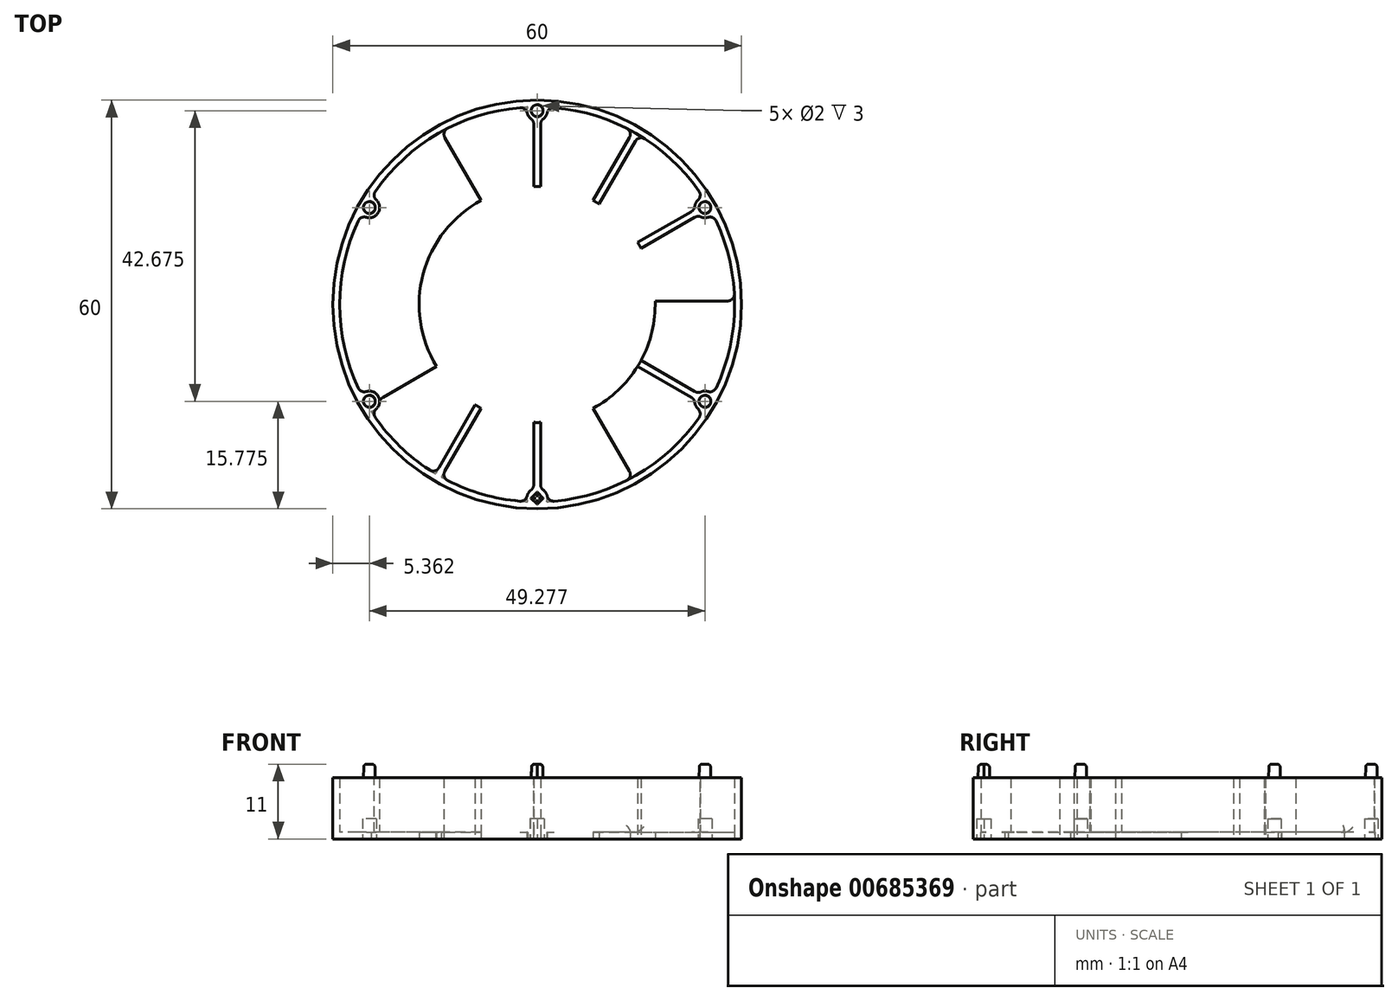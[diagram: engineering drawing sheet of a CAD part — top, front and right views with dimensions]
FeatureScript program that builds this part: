
annotation { "Feature Type Name" : "Feature", "Feature Type Description" : "" }
export const myFeature = defineFeature(function(context is Context, id is Id, definition is map)
    precondition{}
    {
        {
            var Q0;
            Q0=qCreatedBy(makeId("Top.planeOp"),FACE);
            var sketch = newSketch(context, id + "F0", { "sketchPlane" : qUnion([Q0])});
            skCircle(sketch, "E0", {"center": v(0, 0) * mm, "radius": 30 * mm});
            skCircle(sketch, "E1.0", {"center": v(0, 0) * mm, "radius": 29 * mm});
            skLineSegment(sketch, "E2.bottom", {"start": v(14.56, 26.23) * mm, "end": v(15.43, 25.73) * mm});
            skLineSegment(sketch, "E2.top", {"start": v(-15.43, -25.73) * mm, "end": v(-14.56, -26.23) * mm});
            skLineSegment(sketch, "E2.left", {"start": v(14.56, 26.23) * mm, "end": v(-15.43, -25.73) * mm});
            skLineSegment(sketch, "E2.right", {"start": v(15.43, 25.73) * mm, "end": v(-14.56, -26.23) * mm});
            skLineSegment(sketch, "E3.bottom", {"start": v(25.73, 15.43) * mm, "end": v(26.23, 14.56) * mm});
            skLineSegment(sketch, "E3.top", {"start": v(-26.23, -14.56) * mm, "end": v(-25.73, -15.43) * mm});
            skLineSegment(sketch, "E3.left", {"start": v(25.73, 15.43) * mm, "end": v(-26.23, -14.56) * mm});
            skLineSegment(sketch, "E3.right", {"start": v(26.23, 14.56) * mm, "end": v(-25.73, -15.43) * mm});
            skLineSegment(sketch, "E4", {"start": v(-38.35, 0) * mm, "end": v(39.17, 0) * mm, "construction": true});
            skLineSegment(sketch, "E5", {"start": v(0, 42.5) * mm, "end": v(0, -42.47) * mm, "construction": true});
            skLineSegment(sketch, "E6.bottom", {"start": v(-30, 0.5) * mm, "end": v(30, 0.5) * mm});
            skLineSegment(sketch, "E6.top", {"start": v(-30, -0.5) * mm, "end": v(30, -0.5) * mm});
            skLineSegment(sketch, "E6.left", {"start": v(-30, 0.5) * mm, "end": v(-30, -0.5) * mm});
            skLineSegment(sketch, "E6.right", {"start": v(30, 0.5) * mm, "end": v(30, -0.5) * mm});
            skLineSegment(sketch, "E7.bottom", {"start": v(-25.73, 15.43) * mm, "end": v(26.23, -14.56) * mm});
            skLineSegment(sketch, "E7.top", {"start": v(-26.23, 14.56) * mm, "end": v(25.73, -15.43) * mm});
            skLineSegment(sketch, "E7.left", {"start": v(-25.73, 15.43) * mm, "end": v(-26.23, 14.56) * mm});
            skLineSegment(sketch, "E7.right", {"start": v(26.23, -14.56) * mm, "end": v(25.73, -15.43) * mm});
            skLineSegment(sketch, "E8.bottom", {"start": v(-0.5, 30) * mm, "end": v(0.5, 30) * mm});
            skLineSegment(sketch, "E8.top", {"start": v(-0.5, -30) * mm, "end": v(0.5, -30) * mm});
            skLineSegment(sketch, "E8.left", {"start": v(-0.5, 30) * mm, "end": v(-0.5, -30) * mm});
            skLineSegment(sketch, "E8.right", {"start": v(0.5, 30) * mm, "end": v(0.5, -30) * mm});
            skLineSegment(sketch, "E9.bottom", {"start": v(-15.43, 25.73) * mm, "end": v(-14.56, 26.23) * mm});
            skLineSegment(sketch, "E9.top", {"start": v(14.56, -26.23) * mm, "end": v(15.43, -25.73) * mm});
            skLineSegment(sketch, "E9.left", {"start": v(-15.43, 25.73) * mm, "end": v(14.56, -26.23) * mm});
            skLineSegment(sketch, "E9.right", {"start": v(-14.56, 26.23) * mm, "end": v(15.43, -25.73) * mm});
            skCircle(sketch, "E10", {"center": v(0, 0) * mm, "radius": 17.33 * mm});
            skSolve(sketch);
        }
        {
            var Q0;
            Q0=qCreatedBy(makeId("Top.planeOp"),FACE);
            var sketch = newSketch(context, id + "F1", { "sketchPlane" : qUnion([Q0])});
            skCircle(sketch, "E11", {"center": v(0, 0) * mm, "radius": 30 * mm});
            skCircle(sketch, "E12", {"center": v(0, 0) * mm, "radius": 29 * mm});
            skSolve(sketch);
        }
        {
            var Q0;
            Q0=makeQuery(id+"F1.imprint","IMPRINT",FACE,{"disambiguationData":[TD([[makeQuery(id+"F1.imprint","IMPRINT",EDGE,{"derivedFrom":sQuery(id+"F1.wireOp",EDGE,"E11")}),1.0]])]});
            extrude(context, id + "F2", {"entities" : qUnion([Q0]), "depth" : 9 * mm, "offsetDistance" : 25 * mm});
        }
        {
            var Q0;
            {var subQ0=sQuery(id+"F0.wireOp",EDGE,"E8.left");var subQ1=sQuery(id+"F0.wireOp",EDGE,"E1.0");var subQ2=makeQuery(id+"F0.imprint","INTERSECT",VERTEX,{"disambiguationData":[OD(1.0)],"derivedFrom":[subQ1,subQ0]});Q0=makeQuery(id+"F0.imprint","IMPRINT",FACE,{"disambiguationData":[TD([[makeQuery(id+"F0.imprint","IMPRINT",EDGE,{"disambiguationData":[TD([[subQ2,-1.0]])],"derivedFrom":subQ1}),1.0]])]});}
            var Q1;
            {var subQ0=sQuery(id+"F0.wireOp",EDGE,"E8.right");var subQ1=sQuery(id+"F0.wireOp",EDGE,"E1.0");var subQ2=makeQuery(id+"F0.imprint","INTERSECT",VERTEX,{"disambiguationData":[OD(0.0)],"derivedFrom":[subQ1,subQ0]});Q1=makeQuery(id+"F0.imprint","IMPRINT",FACE,{"disambiguationData":[TD([[makeQuery(id+"F0.imprint","IMPRINT",EDGE,{"disambiguationData":[TD([[subQ2,-1.0]])],"derivedFrom":subQ1}),1.0]])]});}
            var Q2;
            {var subQ0=sQuery(id+"F0.wireOp",EDGE,"E3.right");var subQ1=sQuery(id+"F0.wireOp",EDGE,"E1.0");var subQ2=makeQuery(id+"F0.imprint","INTERSECT",VERTEX,{"disambiguationData":[OD(0.0)],"derivedFrom":[subQ1,subQ0]});Q2=makeQuery(id+"F0.imprint","IMPRINT",FACE,{"disambiguationData":[TD([[makeQuery(id+"F0.imprint","IMPRINT",EDGE,{"disambiguationData":[TD([[subQ2,-1.0]])],"derivedFrom":subQ1}),1.0]])]});}
            var Q3;
            {var subQ0=sQuery(id+"F0.wireOp",EDGE,"E7.top");var subQ1=sQuery(id+"F0.wireOp",EDGE,"E1.0");var subQ2=makeQuery(id+"F0.imprint","INTERSECT",VERTEX,{"disambiguationData":[OD(1.0)],"derivedFrom":[subQ1,subQ0]});Q3=makeQuery(id+"F0.imprint","IMPRINT",FACE,{"disambiguationData":[TD([[makeQuery(id+"F0.imprint","IMPRINT",EDGE,{"disambiguationData":[TD([[subQ2,-1.0]])],"derivedFrom":subQ1}),1.0]])]});}
            var Q4;
            {var subQ0=sQuery(id+"F0.wireOp",EDGE,"E2.left");var subQ1=sQuery(id+"F0.wireOp",EDGE,"E1.0");var subQ2=makeQuery(id+"F0.imprint","INTERSECT",VERTEX,{"disambiguationData":[OD(1.0)],"derivedFrom":[subQ1,subQ0]});Q4=makeQuery(id+"F0.imprint","IMPRINT",FACE,{"disambiguationData":[TD([[makeQuery(id+"F0.imprint","IMPRINT",EDGE,{"disambiguationData":[TD([[subQ2,-1.0]])],"derivedFrom":subQ1}),1.0]])]});}
            extrude(context, id + "F3", {"entities" : qUnion([Q0, Q1, Q2, Q3, Q4]), "operationType" : NewBodyOperationType.ADD, "depth" : 9 * mm, "offsetDistance" : 25 * mm});
        }
        {
            var Q0;
            Q0=makeQuery(id+"F1.imprint","IMPRINT",FACE,{"disambiguationData":[TD([[makeQuery(id+"F1.imprint","IMPRINT",EDGE,{"derivedFrom":sQuery(id+"F1.wireOp",EDGE,"E11")}),1.0]])]});
            var Q1;
            Q1=makeQuery(id+"F1.imprint","IMPRINT",FACE,{"disambiguationData":[TD([[makeQuery(id+"F1.imprint","IMPRINT",EDGE,{"derivedFrom":sQuery(id+"F1.wireOp",EDGE,"E12")}),1.0]])]});
            extrude(context, id + "F4", {"entities" : qUnion([Q0, Q1]), "operationType" : NewBodyOperationType.ADD, "depth" : 1 * mm, "offsetDistance" : 25 * mm});
        }
        {
            var Q0;
            {var subQ0=sQuery(id+"F0.wireOp",EDGE,"E8.right");var subQ1=sQuery(id+"F0.wireOp",EDGE,"E1.0");var subQ2=makeQuery(id+"F0.imprint","INTERSECT",VERTEX,{"disambiguationData":[OD(1.0)],"derivedFrom":[subQ1,subQ0]});Q0=makeQuery(id+"F0.imprint","IMPRINT",FACE,{"disambiguationData":[TD([[makeQuery(id+"F0.imprint","IMPRINT",EDGE,{"disambiguationData":[TD([[subQ2,-1.0]])],"derivedFrom":subQ1}),1.0]])]});}
            var Q1;
            {var subQ0=sQuery(id+"F0.wireOp",EDGE,"E3.right");var subQ1=sQuery(id+"F0.wireOp",EDGE,"E1.0");var subQ2=makeQuery(id+"F0.imprint","INTERSECT",VERTEX,{"disambiguationData":[OD(0.0)],"derivedFrom":[subQ1,subQ0]});Q1=makeQuery(id+"F0.imprint","IMPRINT",FACE,{"disambiguationData":[TD([[makeQuery(id+"F0.imprint","IMPRINT",EDGE,{"disambiguationData":[TD([[subQ2,1.0]])],"derivedFrom":subQ1}),1.0]])]});}
            var Q2;
            {var subQ0=sQuery(id+"F0.wireOp",EDGE,"E3.left");var subQ1=sQuery(id+"F0.wireOp",EDGE,"E1.0");var subQ2=makeQuery(id+"F0.imprint","INTERSECT",VERTEX,{"disambiguationData":[OD(0.0)],"derivedFrom":[subQ1,subQ0]});Q2=makeQuery(id+"F0.imprint","IMPRINT",FACE,{"disambiguationData":[TD([[makeQuery(id+"F0.imprint","IMPRINT",EDGE,{"disambiguationData":[TD([[subQ2,-1.0]])],"derivedFrom":subQ1}),1.0]])]});}
            var Q3;
            {var subQ0=sQuery(id+"F0.wireOp",EDGE,"E2.left");var subQ1=sQuery(id+"F0.wireOp",EDGE,"E1.0");var subQ2=makeQuery(id+"F0.imprint","INTERSECT",VERTEX,{"disambiguationData":[OD(0.0)],"derivedFrom":[subQ1,subQ0]});Q3=makeQuery(id+"F0.imprint","IMPRINT",FACE,{"disambiguationData":[TD([[makeQuery(id+"F0.imprint","IMPRINT",EDGE,{"disambiguationData":[TD([[subQ2,-1.0]])],"derivedFrom":subQ1}),1.0]])]});}
            var Q4;
            {var subQ0=sQuery(id+"F0.wireOp",EDGE,"E8.left");var subQ1=sQuery(id+"F0.wireOp",EDGE,"E1.0");var subQ2=makeQuery(id+"F0.imprint","INTERSECT",VERTEX,{"disambiguationData":[OD(0.0)],"derivedFrom":[subQ1,subQ0]});Q4=makeQuery(id+"F0.imprint","IMPRINT",FACE,{"disambiguationData":[TD([[makeQuery(id+"F0.imprint","IMPRINT",EDGE,{"disambiguationData":[TD([[subQ2,-1.0]])],"derivedFrom":subQ1}),1.0]])]});}
            var Q5;
            {var subQ0=sQuery(id+"F0.wireOp",EDGE,"E3.right");var subQ1=sQuery(id+"F0.wireOp",EDGE,"E1.0");var subQ2=makeQuery(id+"F0.imprint","INTERSECT",VERTEX,{"disambiguationData":[OD(1.0)],"derivedFrom":[subQ1,subQ0]});Q5=makeQuery(id+"F0.imprint","IMPRINT",FACE,{"disambiguationData":[TD([[makeQuery(id+"F0.imprint","IMPRINT",EDGE,{"disambiguationData":[TD([[subQ2,-1.0]])],"derivedFrom":subQ1}),1.0]])]});}
            var Q6;
            {var subQ0=sQuery(id+"F0.wireOp",EDGE,"E2.right");var subQ1=sQuery(id+"F0.wireOp",EDGE,"E1.0");var subQ2=makeQuery(id+"F0.imprint","INTERSECT",VERTEX,{"disambiguationData":[OD(1.0)],"derivedFrom":[subQ1,subQ0]});Q6=makeQuery(id+"F0.imprint","IMPRINT",FACE,{"disambiguationData":[TD([[makeQuery(id+"F0.imprint","IMPRINT",EDGE,{"disambiguationData":[TD([[subQ2,-1.0]])],"derivedFrom":subQ1}),1.0]])]});}
            extrude(context, id + "F5", {"entities" : qUnion([Q0, Q1, Q2, Q3, Q4, Q5, Q6]), "operationType" : NewBodyOperationType.REMOVE, "depth" : 1 * mm, "offsetDistance" : 25 * mm});
        }
        {
            var Q0;
            Q0=qCreatedBy(makeId("Top.planeOp"),FACE);
            var sketch = newSketch(context, id + "F6", { "sketchPlane" : qUnion([Q0])});
            skCircle(sketch, "E13", {"center": v(0, 0) * mm, "radius": 28.45 * mm});
            skLineSegment(sketch, "E14", {"start": v(0, 28.45) * mm, "end": v(0, -28.45) * mm, "construction": true});
            skLineSegment(sketch, "E15", {"start": v(24.64, 14.22) * mm, "end": v(0, 0) * mm, "construction": true});
            skLineSegment(sketch, "E16", {"start": v(14.23, 24.64) * mm, "end": v(0, 0) * mm, "construction": true});
            skLineSegment(sketch, "E17", {"start": v(0, 0) * mm, "end": v(28.45, 0) * mm, "construction": true});
            skLineSegment(sketch, "E18", {"start": v(0, 0) * mm, "end": v(24.64, -14.22) * mm, "construction": true});
            skLineSegment(sketch, "E19", {"start": v(0, 0) * mm, "end": v(14.23, -24.64) * mm, "construction": true});
            skLineSegment(sketch, "E20", {"start": v(0, 0) * mm, "end": v(-14.23, 24.64) * mm, "construction": true});
            skLineSegment(sketch, "E21", {"start": v(0, 0) * mm, "end": v(-24.64, 14.22) * mm, "construction": true});
            skLineSegment(sketch, "E22", {"start": v(0, 0) * mm, "end": v(-28.45, 0) * mm, "construction": true});
            skLineSegment(sketch, "E23", {"start": v(0, 0) * mm, "end": v(-24.64, -14.23) * mm, "construction": true});
            skLineSegment(sketch, "E24", {"start": v(0, 0) * mm, "end": v(-14.22, -24.64) * mm, "construction": true});
            skCircle(sketch, "E25", {"center": v(0, 28.45) * mm, "radius": 1.5 * mm});
            skCircle(sketch, "E26", {"center": v(24.64, 14.22) * mm, "radius": 1.5 * mm});
            skCircle(sketch, "E27", {"center": v(24.64, -14.22) * mm, "radius": 1.5 * mm});
            skCircle(sketch, "E28", {"center": v(0, -28.45) * mm, "radius": 1.5 * mm});
            skCircle(sketch, "E29", {"center": v(-24.64, -14.23) * mm, "radius": 1.5 * mm});
            skCircle(sketch, "E30", {"center": v(-24.64, 14.22) * mm, "radius": 1.5 * mm});
            skCircle(sketch, "E31", {"center": v(-24.64, 14.22) * mm, "radius": 1 * mm});
            skCircle(sketch, "E32", {"center": v(0, 28.45) * mm, "radius": 1 * mm});
            skCircle(sketch, "E33", {"center": v(24.64, 14.22) * mm, "radius": 1 * mm});
            skCircle(sketch, "E34", {"center": v(24.64, -14.22) * mm, "radius": 1 * mm});
            skCircle(sketch, "E35", {"center": v(-24.64, -14.23) * mm, "radius": 1 * mm});
            skLineSegment(sketch, "E36.bottom", {"start": v(1.06, -28.45) * mm, "end": v(0, -29.51) * mm});
            skLineSegment(sketch, "E36.top", {"start": v(0, -27.39) * mm, "end": v(-1.06, -28.45) * mm});
            skLineSegment(sketch, "E36.left", {"start": v(1.06, -28.45) * mm, "end": v(0, -27.39) * mm});
            skLineSegment(sketch, "E36.right", {"start": v(0, -29.51) * mm, "end": v(-1.06, -28.45) * mm});
            skSolve(sketch);
        }
        {
            var Q0;
            {var subQ0=sQuery(id+"F6.wireOp",EDGE,"E30");var subQ1=sQuery(id+"F6.wireOp",EDGE,"E13");var subQ2=makeQuery(id+"F6.imprint","INTERSECT",VERTEX,{"disambiguationData":[OD(0.0)],"derivedFrom":[subQ1,subQ0]});Q0=makeQuery(id+"F6.imprint","IMPRINT",FACE,{"disambiguationData":[TD([[makeQuery(id+"F6.imprint","IMPRINT",EDGE,{"disambiguationData":[TD([[subQ2,-1.0]])],"derivedFrom":subQ1}),1.0]])]});}
            var Q1;
            {var subQ0=sQuery(id+"F6.wireOp",EDGE,"E30");var subQ1=sQuery(id+"F6.wireOp",EDGE,"E13");var subQ2=makeQuery(id+"F6.imprint","INTERSECT",VERTEX,{"disambiguationData":[OD(0.0)],"derivedFrom":[subQ1,subQ0]});Q1=makeQuery(id+"F6.imprint","IMPRINT",FACE,{"disambiguationData":[TD([[makeQuery(id+"F6.imprint","IMPRINT",EDGE,{"disambiguationData":[TD([[subQ2,-1.0]])],"derivedFrom":subQ1}),-1.0]])]});}
            var Q2;
            {var subQ0=sQuery(id+"F6.wireOp",EDGE,"E25");var subQ1=sQuery(id+"F6.wireOp",EDGE,"E13");var subQ2=makeQuery(id+"F6.imprint","INTERSECT",VERTEX,{"disambiguationData":[OD(0.0)],"derivedFrom":[subQ1,subQ0]});Q2=makeQuery(id+"F6.imprint","IMPRINT",FACE,{"disambiguationData":[TD([[makeQuery(id+"F6.imprint","IMPRINT",EDGE,{"disambiguationData":[TD([[subQ2,-1.0]])],"derivedFrom":subQ1}),1.0]])]});}
            var Q3;
            {var subQ0=sQuery(id+"F6.wireOp",EDGE,"E25");var subQ1=sQuery(id+"F6.wireOp",EDGE,"E13");var subQ2=makeQuery(id+"F6.imprint","INTERSECT",VERTEX,{"disambiguationData":[OD(0.0)],"derivedFrom":[subQ1,subQ0]});Q3=makeQuery(id+"F6.imprint","IMPRINT",FACE,{"disambiguationData":[TD([[makeQuery(id+"F6.imprint","IMPRINT",EDGE,{"disambiguationData":[TD([[subQ2,-1.0]])],"derivedFrom":subQ1}),-1.0]])]});}
            var Q4;
            {var subQ0=sQuery(id+"F6.wireOp",EDGE,"E26");var subQ1=sQuery(id+"F6.wireOp",EDGE,"E13");var subQ2=makeQuery(id+"F6.imprint","INTERSECT",VERTEX,{"disambiguationData":[OD(0.0)],"derivedFrom":[subQ1,subQ0]});Q4=makeQuery(id+"F6.imprint","IMPRINT",FACE,{"disambiguationData":[TD([[makeQuery(id+"F6.imprint","IMPRINT",EDGE,{"disambiguationData":[TD([[subQ2,-1.0]])],"derivedFrom":subQ1}),-1.0]])]});}
            var Q5;
            {var subQ0=sQuery(id+"F6.wireOp",EDGE,"E26");var subQ1=sQuery(id+"F6.wireOp",EDGE,"E13");var subQ2=makeQuery(id+"F6.imprint","INTERSECT",VERTEX,{"disambiguationData":[OD(0.0)],"derivedFrom":[subQ1,subQ0]});Q5=makeQuery(id+"F6.imprint","IMPRINT",FACE,{"disambiguationData":[TD([[makeQuery(id+"F6.imprint","IMPRINT",EDGE,{"disambiguationData":[TD([[subQ2,-1.0]])],"derivedFrom":subQ1}),1.0]])]});}
            var Q6;
            {var subQ0=sQuery(id+"F6.wireOp",EDGE,"E29");var subQ1=sQuery(id+"F6.wireOp",EDGE,"E13");var subQ2=makeQuery(id+"F6.imprint","INTERSECT",VERTEX,{"disambiguationData":[OD(0.0)],"derivedFrom":[subQ1,subQ0]});Q6=makeQuery(id+"F6.imprint","IMPRINT",FACE,{"disambiguationData":[TD([[makeQuery(id+"F6.imprint","IMPRINT",EDGE,{"disambiguationData":[TD([[subQ2,-1.0]])],"derivedFrom":subQ1}),1.0]])]});}
            var Q7;
            {var subQ0=sQuery(id+"F6.wireOp",EDGE,"E29");var subQ1=sQuery(id+"F6.wireOp",EDGE,"E13");var subQ2=makeQuery(id+"F6.imprint","INTERSECT",VERTEX,{"disambiguationData":[OD(0.0)],"derivedFrom":[subQ1,subQ0]});Q7=makeQuery(id+"F6.imprint","IMPRINT",FACE,{"disambiguationData":[TD([[makeQuery(id+"F6.imprint","IMPRINT",EDGE,{"disambiguationData":[TD([[subQ2,-1.0]])],"derivedFrom":subQ1}),-1.0]])]});}
            var Q8;
            {var subQ3=sQuery(id+"F6.wireOp",EDGE,"E13");var subQ5=sQuery(id+"F6.wireOp",EDGE,"E28");var subQ6=makeQuery(id+"F6.imprint","INTERSECT",VERTEX,{"disambiguationData":[OD(0.0)],"derivedFrom":[subQ3,subQ5]});Q8=makeQuery(id+"F6.imprint","IMPRINT",FACE,{"disambiguationData":[TD([[makeQuery(id+"F6.imprint","IMPRINT",EDGE,{"disambiguationData":[TD([[subQ6,-1.0]])],"derivedFrom":subQ3}),1.0]])]});}
            var Q9;
            {var subQ6=sQuery(id+"F6.wireOp",EDGE,"E36.bottom");Q9=makeQuery(id+"F6.imprint","IMPRINT",FACE,{"disambiguationData":[TD([[makeQuery(id+"F6.imprint","IMPRINT",EDGE,{"derivedFrom":subQ6}),1.0]])]});}
            var Q10;
            {var subQ0=sQuery(id+"F6.wireOp",EDGE,"E27");var subQ1=sQuery(id+"F6.wireOp",EDGE,"E13");var subQ2=makeQuery(id+"F6.imprint","INTERSECT",VERTEX,{"disambiguationData":[OD(0.0)],"derivedFrom":[subQ1,subQ0]});Q10=makeQuery(id+"F6.imprint","IMPRINT",FACE,{"disambiguationData":[TD([[makeQuery(id+"F6.imprint","IMPRINT",EDGE,{"disambiguationData":[TD([[subQ2,-1.0]])],"derivedFrom":subQ1}),-1.0]])]});}
            var Q11;
            {var subQ0=sQuery(id+"F6.wireOp",EDGE,"E27");var subQ1=sQuery(id+"F6.wireOp",EDGE,"E13");var subQ2=makeQuery(id+"F6.imprint","INTERSECT",VERTEX,{"disambiguationData":[OD(0.0)],"derivedFrom":[subQ1,subQ0]});Q11=makeQuery(id+"F6.imprint","IMPRINT",FACE,{"disambiguationData":[TD([[makeQuery(id+"F6.imprint","IMPRINT",EDGE,{"disambiguationData":[TD([[subQ2,-1.0]])],"derivedFrom":subQ1}),1.0]])]});}
            var Q12;
            {var subQ0=sQuery(id+"F6.wireOp",EDGE,"E31");var subQ1=sQuery(id+"F6.wireOp",EDGE,"E13");var subQ2=makeQuery(id+"F6.imprint","INTERSECT",VERTEX,{"disambiguationData":[OD(0.0)],"derivedFrom":[subQ1,subQ0]});Q12=makeQuery(id+"F6.imprint","IMPRINT",FACE,{"disambiguationData":[TD([[makeQuery(id+"F6.imprint","IMPRINT",EDGE,{"disambiguationData":[TD([[subQ2,-1.0]])],"derivedFrom":subQ1}),1.0]])]});}
            var Q13;
            {var subQ0=sQuery(id+"F6.wireOp",EDGE,"E31");var subQ1=sQuery(id+"F6.wireOp",EDGE,"E13");var subQ2=makeQuery(id+"F6.imprint","INTERSECT",VERTEX,{"disambiguationData":[OD(0.0)],"derivedFrom":[subQ1,subQ0]});Q13=makeQuery(id+"F6.imprint","IMPRINT",FACE,{"disambiguationData":[TD([[makeQuery(id+"F6.imprint","IMPRINT",EDGE,{"disambiguationData":[TD([[subQ2,-1.0]])],"derivedFrom":subQ1}),-1.0]])]});}
            var Q14;
            {var subQ0=sQuery(id+"F6.wireOp",EDGE,"E32");var subQ1=sQuery(id+"F6.wireOp",EDGE,"E13");var subQ2=makeQuery(id+"F6.imprint","INTERSECT",VERTEX,{"disambiguationData":[OD(0.0)],"derivedFrom":[subQ1,subQ0]});Q14=makeQuery(id+"F6.imprint","IMPRINT",FACE,{"disambiguationData":[TD([[makeQuery(id+"F6.imprint","IMPRINT",EDGE,{"disambiguationData":[TD([[subQ2,-1.0]])],"derivedFrom":subQ1}),-1.0]])]});}
            var Q15;
            {var subQ0=sQuery(id+"F6.wireOp",EDGE,"E32");var subQ1=sQuery(id+"F6.wireOp",EDGE,"E13");var subQ2=makeQuery(id+"F6.imprint","INTERSECT",VERTEX,{"disambiguationData":[OD(0.0)],"derivedFrom":[subQ1,subQ0]});Q15=makeQuery(id+"F6.imprint","IMPRINT",FACE,{"disambiguationData":[TD([[makeQuery(id+"F6.imprint","IMPRINT",EDGE,{"disambiguationData":[TD([[subQ2,-1.0]])],"derivedFrom":subQ1}),1.0]])]});}
            var Q16;
            {var subQ0=sQuery(id+"F6.wireOp",EDGE,"E33");var subQ1=sQuery(id+"F6.wireOp",EDGE,"E13");var subQ2=makeQuery(id+"F6.imprint","INTERSECT",VERTEX,{"disambiguationData":[OD(0.0)],"derivedFrom":[subQ1,subQ0]});Q16=makeQuery(id+"F6.imprint","IMPRINT",FACE,{"disambiguationData":[TD([[makeQuery(id+"F6.imprint","IMPRINT",EDGE,{"disambiguationData":[TD([[subQ2,-1.0]])],"derivedFrom":subQ1}),-1.0]])]});}
            var Q17;
            {var subQ0=sQuery(id+"F6.wireOp",EDGE,"E33");var subQ1=sQuery(id+"F6.wireOp",EDGE,"E13");var subQ2=makeQuery(id+"F6.imprint","INTERSECT",VERTEX,{"disambiguationData":[OD(0.0)],"derivedFrom":[subQ1,subQ0]});Q17=makeQuery(id+"F6.imprint","IMPRINT",FACE,{"disambiguationData":[TD([[makeQuery(id+"F6.imprint","IMPRINT",EDGE,{"disambiguationData":[TD([[subQ2,-1.0]])],"derivedFrom":subQ1}),1.0]])]});}
            var Q18;
            {var subQ0=sQuery(id+"F6.wireOp",EDGE,"E34");var subQ1=sQuery(id+"F6.wireOp",EDGE,"E13");var subQ2=makeQuery(id+"F6.imprint","INTERSECT",VERTEX,{"disambiguationData":[OD(0.0)],"derivedFrom":[subQ1,subQ0]});Q18=makeQuery(id+"F6.imprint","IMPRINT",FACE,{"disambiguationData":[TD([[makeQuery(id+"F6.imprint","IMPRINT",EDGE,{"disambiguationData":[TD([[subQ2,-1.0]])],"derivedFrom":subQ1}),-1.0]])]});}
            var Q19;
            {var subQ0=sQuery(id+"F6.wireOp",EDGE,"E34");var subQ1=sQuery(id+"F6.wireOp",EDGE,"E13");var subQ2=makeQuery(id+"F6.imprint","INTERSECT",VERTEX,{"disambiguationData":[OD(0.0)],"derivedFrom":[subQ1,subQ0]});Q19=makeQuery(id+"F6.imprint","IMPRINT",FACE,{"disambiguationData":[TD([[makeQuery(id+"F6.imprint","IMPRINT",EDGE,{"disambiguationData":[TD([[subQ2,-1.0]])],"derivedFrom":subQ1}),1.0]])]});}
            var Q20;
            {var subQ1=sQuery(id+"F6.wireOp",EDGE,"E36.bottom");Q20=makeQuery(id+"F6.imprint","IMPRINT",FACE,{"disambiguationData":[TD([[makeQuery(id+"F6.imprint","IMPRINT",EDGE,{"derivedFrom":subQ1}),-1.0]])]});}
            var Q21;
            {var subQ0=sQuery(id+"F6.wireOp",EDGE,"E35");var subQ1=sQuery(id+"F6.wireOp",EDGE,"E13");var subQ2=makeQuery(id+"F6.imprint","INTERSECT",VERTEX,{"disambiguationData":[OD(0.0)],"derivedFrom":[subQ1,subQ0]});Q21=makeQuery(id+"F6.imprint","IMPRINT",FACE,{"disambiguationData":[TD([[makeQuery(id+"F6.imprint","IMPRINT",EDGE,{"disambiguationData":[TD([[subQ2,-1.0]])],"derivedFrom":subQ1}),-1.0]])]});}
            var Q22;
            {var subQ0=sQuery(id+"F6.wireOp",EDGE,"E35");var subQ1=sQuery(id+"F6.wireOp",EDGE,"E13");var subQ2=makeQuery(id+"F6.imprint","INTERSECT",VERTEX,{"disambiguationData":[OD(0.0)],"derivedFrom":[subQ1,subQ0]});Q22=makeQuery(id+"F6.imprint","IMPRINT",FACE,{"disambiguationData":[TD([[makeQuery(id+"F6.imprint","IMPRINT",EDGE,{"disambiguationData":[TD([[subQ2,-1.0]])],"derivedFrom":subQ1}),1.0]])]});}
            var Q23;
            {var subQ0=sQuery(id+"F6.wireOp",EDGE,"E36.top");var subQ1=sQuery(id+"F6.wireOp",EDGE,"E13");var subQ2=makeQuery(id+"F6.imprint","INTERSECT",VERTEX,{"derivedFrom":[subQ1,subQ0]});Q23=makeQuery(id+"F6.imprint","IMPRINT",FACE,{"disambiguationData":[TD([[makeQuery(id+"F6.imprint","IMPRINT",EDGE,{"disambiguationData":[TD([[subQ2,-1.0]])],"derivedFrom":subQ1}),1.0]])]});}
            extrude(context, id + "F7", {"entities" : qUnion([Q0, Q1, Q2, Q3, Q4, Q5, Q6, Q7, Q8, Q9, Q10, Q11, Q12, Q13, Q14, Q15, Q16, Q17, Q18, Q19, Q20, Q21, Q22, Q23]), "operationType" : NewBodyOperationType.ADD, "depth" : 9 * mm, "offsetDistance" : 25 * mm});
        }
        {
            var Q0;
            {var subQ0=sQuery(id+"F0.wireOp",EDGE,"E8.right");var subQ1=sQuery(id+"F0.wireOp",EDGE,"E1.0");Q0=makeQuery(id+"F3.opExtrude","SWEPT_EDGE",EDGE,{"disambiguationData":[OSD([subQ1,subQ0]),TDD([makeQuery(id+"F0.imprint","INTERSECT",VERTEX,{"disambiguationData":[OD(1.0)],"derivedFrom":[subQ1,subQ0]})])]});}
            var Q1;
            {var subQ0=sQuery(id+"F0.wireOp",EDGE,"E2.left");var subQ1=sQuery(id+"F0.wireOp",EDGE,"E1.0");Q1=makeQuery(id+"F3.opExtrude","SWEPT_EDGE",EDGE,{"disambiguationData":[OSD([subQ1,subQ0]),TDD([makeQuery(id+"F0.imprint","INTERSECT",VERTEX,{"disambiguationData":[OD(1.0)],"derivedFrom":[subQ1,subQ0]})])]});}
            var Q2;
            {var subQ0=sQuery(id+"F0.wireOp",EDGE,"E3.left");var subQ1=sQuery(id+"F0.wireOp",EDGE,"E1.0");Q2=makeQuery(id+"F3.opExtrude","SWEPT_EDGE",EDGE,{"disambiguationData":[OSD([subQ1,subQ0]),TDD([makeQuery(id+"F0.imprint","INTERSECT",VERTEX,{"disambiguationData":[OD(1.0)],"derivedFrom":[subQ1,subQ0]})])]});}
            var Q3;
            {var subQ0=sQuery(id+"F0.wireOp",EDGE,"E6.bottom");var subQ1=sQuery(id+"F0.wireOp",EDGE,"E1.0");Q3=makeQuery(id+"F3.opExtrude","SWEPT_EDGE",EDGE,{"disambiguationData":[OSD([subQ1,subQ0]),TDD([makeQuery(id+"F0.imprint","INTERSECT",VERTEX,{"disambiguationData":[OD(1.0)],"derivedFrom":[subQ1,subQ0]})])]});}
            var Q4;
            {var subQ0=sQuery(id+"F0.wireOp",EDGE,"E9.right");var subQ1=sQuery(id+"F0.wireOp",EDGE,"E1.0");Q4=makeQuery(id+"F3.opExtrude","SWEPT_EDGE",EDGE,{"disambiguationData":[OSD([subQ1,subQ0]),TDD([makeQuery(id+"F0.imprint","INTERSECT",VERTEX,{"disambiguationData":[OD(1.0)],"derivedFrom":[subQ1,subQ0]})])]});}
            var Q5;
            {var subQ0=sQuery(id+"F0.wireOp",EDGE,"E7.bottom");var subQ1=sQuery(id+"F0.wireOp",EDGE,"E1.0");Q5=makeQuery(id+"F3.opExtrude","SWEPT_EDGE",EDGE,{"disambiguationData":[OSD([subQ1,subQ0]),TDD([makeQuery(id+"F0.imprint","INTERSECT",VERTEX,{"disambiguationData":[OD(1.0)],"derivedFrom":[subQ1,subQ0]})])]});}
            var Q6;
            {var subQ0=sQuery(id+"F0.wireOp",EDGE,"E8.left");var subQ1=sQuery(id+"F0.wireOp",EDGE,"E1.0");Q6=makeQuery(id+"F3.opExtrude","SWEPT_EDGE",EDGE,{"disambiguationData":[OSD([subQ1,subQ0]),TDD([makeQuery(id+"F0.imprint","INTERSECT",VERTEX,{"disambiguationData":[OD(0.0)],"derivedFrom":[subQ1,subQ0]})])]});}
            var Q7;
            {var subQ0=sQuery(id+"F0.wireOp",EDGE,"E2.left");var subQ1=sQuery(id+"F0.wireOp",EDGE,"E1.0");Q7=makeQuery(id+"F3.opExtrude","SWEPT_EDGE",EDGE,{"disambiguationData":[OSD([subQ1,subQ0]),TDD([makeQuery(id+"F0.imprint","INTERSECT",VERTEX,{"disambiguationData":[OD(0.0)],"derivedFrom":[subQ1,subQ0]})])]});}
            var Q8;
            {var subQ0=sQuery(id+"F0.wireOp",EDGE,"E3.left");var subQ1=sQuery(id+"F0.wireOp",EDGE,"E1.0");Q8=makeQuery(id+"F3.opExtrude","SWEPT_EDGE",EDGE,{"disambiguationData":[OSD([subQ1,subQ0]),TDD([makeQuery(id+"F0.imprint","INTERSECT",VERTEX,{"disambiguationData":[OD(0.0)],"derivedFrom":[subQ1,subQ0]})])]});}
            var Q9;
            {var subQ0=sQuery(id+"F0.wireOp",EDGE,"E6.top");var subQ1=sQuery(id+"F0.wireOp",EDGE,"E1.0");Q9=makeQuery(id+"F3.opExtrude","SWEPT_EDGE",EDGE,{"disambiguationData":[OSD([subQ1,subQ0]),TDD([makeQuery(id+"F0.imprint","INTERSECT",VERTEX,{"disambiguationData":[OD(1.0)],"derivedFrom":[subQ1,subQ0]})])]});}
            var Q10;
            {var subQ0=sQuery(id+"F0.wireOp",EDGE,"E7.top");var subQ1=sQuery(id+"F0.wireOp",EDGE,"E1.0");Q10=makeQuery(id+"F3.opExtrude","SWEPT_EDGE",EDGE,{"disambiguationData":[OSD([subQ1,subQ0]),TDD([makeQuery(id+"F0.imprint","INTERSECT",VERTEX,{"disambiguationData":[OD(0.0)],"derivedFrom":[subQ1,subQ0]})])]});}
            var Q11;
            {var subQ0=sQuery(id+"F0.wireOp",EDGE,"E6.top");var subQ1=sQuery(id+"F0.wireOp",EDGE,"E1.0");Q11=makeQuery(id+"F3.opExtrude","SWEPT_EDGE",EDGE,{"disambiguationData":[OSD([subQ1,subQ0]),TDD([makeQuery(id+"F0.imprint","INTERSECT",VERTEX,{"disambiguationData":[OD(0.0)],"derivedFrom":[subQ1,subQ0]})])]});}
            var Q12;
            {var subQ0=sQuery(id+"F0.wireOp",EDGE,"E9.left");var subQ1=sQuery(id+"F0.wireOp",EDGE,"E1.0");Q12=makeQuery(id+"F3.opExtrude","SWEPT_EDGE",EDGE,{"disambiguationData":[OSD([subQ1,subQ0]),TDD([makeQuery(id+"F0.imprint","INTERSECT",VERTEX,{"disambiguationData":[OD(0.0)],"derivedFrom":[subQ1,subQ0]})])]});}
            var Q13;
            {var subQ0=sQuery(id+"F0.wireOp",EDGE,"E8.right");var subQ1=sQuery(id+"F0.wireOp",EDGE,"E1.0");Q13=makeQuery(id+"F3.opExtrude","SWEPT_EDGE",EDGE,{"disambiguationData":[OSD([subQ1,subQ0]),TDD([makeQuery(id+"F0.imprint","INTERSECT",VERTEX,{"disambiguationData":[OD(0.0)],"derivedFrom":[subQ1,subQ0]})])]});}
            var Q14;
            {var subQ0=sQuery(id+"F0.wireOp",EDGE,"E7.bottom");var subQ1=sQuery(id+"F0.wireOp",EDGE,"E1.0");Q14=makeQuery(id+"F3.opExtrude","SWEPT_EDGE",EDGE,{"disambiguationData":[OSD([subQ1,subQ0]),TDD([makeQuery(id+"F0.imprint","INTERSECT",VERTEX,{"disambiguationData":[OD(0.0)],"derivedFrom":[subQ1,subQ0]})])]});}
            var Q15;
            {var subQ0=sQuery(id+"F0.wireOp",EDGE,"E9.right");var subQ1=sQuery(id+"F0.wireOp",EDGE,"E1.0");Q15=makeQuery(id+"F3.opExtrude","SWEPT_EDGE",EDGE,{"disambiguationData":[OSD([subQ1,subQ0]),TDD([makeQuery(id+"F0.imprint","INTERSECT",VERTEX,{"disambiguationData":[OD(0.0)],"derivedFrom":[subQ1,subQ0]})])]});}
            var Q16;
            {var subQ0=sQuery(id+"F0.wireOp",EDGE,"E3.right");var subQ1=sQuery(id+"F0.wireOp",EDGE,"E1.0");Q16=makeQuery(id+"F3.opExtrude","SWEPT_EDGE",EDGE,{"disambiguationData":[OSD([subQ1,subQ0]),TDD([makeQuery(id+"F0.imprint","INTERSECT",VERTEX,{"disambiguationData":[OD(1.0)],"derivedFrom":[subQ1,subQ0]})])]});}
            var Q17;
            {var subQ0=sQuery(id+"F0.wireOp",EDGE,"E2.right");var subQ1=sQuery(id+"F0.wireOp",EDGE,"E1.0");Q17=makeQuery(id+"F3.opExtrude","SWEPT_EDGE",EDGE,{"disambiguationData":[OSD([subQ1,subQ0]),TDD([makeQuery(id+"F0.imprint","INTERSECT",VERTEX,{"disambiguationData":[OD(1.0)],"derivedFrom":[subQ1,subQ0]})])]});}
            var Q18;
            {var subQ0=sQuery(id+"F0.wireOp",EDGE,"E3.right");var subQ1=sQuery(id+"F0.wireOp",EDGE,"E1.0");Q18=makeQuery(id+"F3.opExtrude","SWEPT_EDGE",EDGE,{"disambiguationData":[OSD([subQ1,subQ0]),TDD([makeQuery(id+"F0.imprint","INTERSECT",VERTEX,{"disambiguationData":[OD(0.0)],"derivedFrom":[subQ1,subQ0]})])]});}
            var Q19;
            {var subQ0=sQuery(id+"F0.wireOp",EDGE,"E2.right");var subQ1=sQuery(id+"F0.wireOp",EDGE,"E1.0");Q19=makeQuery(id+"F3.opExtrude","SWEPT_EDGE",EDGE,{"disambiguationData":[OSD([subQ1,subQ0]),TDD([makeQuery(id+"F0.imprint","INTERSECT",VERTEX,{"disambiguationData":[OD(0.0)],"derivedFrom":[subQ1,subQ0]})])]});}
            var Q20;
            {var subQ0=sQuery(id+"F0.wireOp",EDGE,"E8.left");var subQ1=sQuery(id+"F0.wireOp",EDGE,"E1.0");Q20=makeQuery(id+"F3.opExtrude","SWEPT_EDGE",EDGE,{"disambiguationData":[OSD([subQ1,subQ0]),TDD([makeQuery(id+"F0.imprint","INTERSECT",VERTEX,{"disambiguationData":[OD(1.0)],"derivedFrom":[subQ1,subQ0]})])]});}
            var Q21;
            {var subQ0=sQuery(id+"F0.wireOp",EDGE,"E9.left");var subQ1=sQuery(id+"F0.wireOp",EDGE,"E1.0");Q21=makeQuery(id+"F3.opExtrude","SWEPT_EDGE",EDGE,{"disambiguationData":[OSD([subQ1,subQ0]),TDD([makeQuery(id+"F0.imprint","INTERSECT",VERTEX,{"disambiguationData":[OD(1.0)],"derivedFrom":[subQ1,subQ0]})])]});}
            var Q22;
            {var subQ0=sQuery(id+"F0.wireOp",EDGE,"E7.top");var subQ1=sQuery(id+"F0.wireOp",EDGE,"E1.0");Q22=makeQuery(id+"F3.opExtrude","SWEPT_EDGE",EDGE,{"disambiguationData":[OSD([subQ1,subQ0]),TDD([makeQuery(id+"F0.imprint","INTERSECT",VERTEX,{"disambiguationData":[OD(1.0)],"derivedFrom":[subQ1,subQ0]})])]});}
            var Q23;
            {var subQ0=sQuery(id+"F0.wireOp",EDGE,"E6.bottom");var subQ1=sQuery(id+"F0.wireOp",EDGE,"E1.0");Q23=makeQuery(id+"F3.opExtrude","SWEPT_EDGE",EDGE,{"disambiguationData":[OSD([subQ1,subQ0]),TDD([makeQuery(id+"F0.imprint","INTERSECT",VERTEX,{"disambiguationData":[OD(0.0)],"derivedFrom":[subQ1,subQ0]})])]});}
            var Q24;
            {var subQ0=sQuery(id+"F0.wireOp",EDGE,"E3.right");var subQ1=sQuery(id+"F0.wireOp",EDGE,"E1.0");var subQ2=sQuery(id+"F0.wireOp",EDGE,"E2.left");var subQ3=sQuery(id+"F0.wireOp",EDGE,"E8.left");var subQ4=makeQuery(id+"F0.imprint","INTERSECT",VERTEX,{"disambiguationData":[OD(0.0)],"derivedFrom":[subQ1,subQ3]});var subQ23=sQuery(id+"F1.wireOp",EDGE,"E12");Q24=makeQuery(id+"F7.boolean.opBoolean","INTERSECT",EDGE,{"disambiguationData":[OD(0.0)],"derivedFrom":[makeQuery(id+"F5.boolean.opBoolean","MERGE",FACE,{"derivedFrom":[makeQuery(id+"F3.boolean.opBoolean","SPLIT",FACE,{"disambiguationData":[TD([makeQuery(id+"F3.opExtrude","SWEPT_FACE",FACE,{"disambiguationData":[OSD([subQ2])]})])],"derivedFrom":makeQuery(id+"F2.opExtrude","SWEPT_FACE",FACE,{"disambiguationData":[OSD([subQ23])]})}),makeQuery(id+"F5.opExtrude","SWEPT_FACE",FACE,{"disambiguationData":[OSD([subQ1]),TDD([makeQuery(id+"F0.imprint","IMPRINT",EDGE,{"disambiguationData":[TD([[subQ4,-1.0]])],"derivedFrom":subQ1})])]}),makeQuery(id+"F5.opExtrude","SWEPT_FACE",FACE,{"disambiguationData":[OSD([subQ1]),TDD([makeQuery(id+"F0.imprint","IMPRINT",EDGE,{"disambiguationData":[TD([[makeQuery(id+"F0.imprint","INTERSECT",VERTEX,{"disambiguationData":[OD(1.0)],"derivedFrom":[subQ1,subQ0]}),-1.0]])],"derivedFrom":subQ1})])]})]}),makeQuery(id+"F7.opExtrude","SWEPT_FACE",FACE,{"disambiguationData":[OSD([sQuery(id+"F6.wireOp",EDGE,"E30")])]})]});}
            var Q25;
            {var subQ0=sQuery(id+"F0.wireOp",EDGE,"E8.right");var subQ1=makeQuery(id+"F0.imprint","IMPRINT",EDGE,{"disambiguationData":[TD([[makeQuery(id+"F0.imprint","INTERSECT",VERTEX,{"disambiguationData":[OD(0.0)],"derivedFrom":[sQuery(id+"F0.wireOp",EDGE,"E1.0"),subQ0]}),-1.0]])],"derivedFrom":subQ0});Q25=makeQuery(id+"F7.boolean.opBoolean","INTERSECT",EDGE,{"derivedFrom":[makeQuery(id+"F5.boolean.opBoolean","MERGE",FACE,{"derivedFrom":[makeQuery(id+"F3.opExtrude","SWEPT_FACE",FACE,{"disambiguationData":[OSD([subQ0]),TDD([subQ1])]}),makeQuery(id+"F5.opExtrude","SWEPT_FACE",FACE,{"disambiguationData":[OSD([subQ0]),TDD([subQ1])]})]}),makeQuery(id+"F7.opExtrude","SWEPT_FACE",FACE,{"disambiguationData":[OSD([sQuery(id+"F6.wireOp",EDGE,"E25")])]})]});}
            var Q26;
            {var subQ0=sQuery(id+"F0.wireOp",EDGE,"E3.right");var subQ1=sQuery(id+"F0.wireOp",EDGE,"E1.0");var subQ2=sQuery(id+"F0.wireOp",EDGE,"E2.left");var subQ3=sQuery(id+"F0.wireOp",EDGE,"E8.left");var subQ4=makeQuery(id+"F0.imprint","INTERSECT",VERTEX,{"disambiguationData":[OD(0.0)],"derivedFrom":[subQ1,subQ3]});var subQ23=sQuery(id+"F1.wireOp",EDGE,"E12");Q26=makeQuery(id+"F7.boolean.opBoolean","INTERSECT",EDGE,{"disambiguationData":[OD(0.0)],"derivedFrom":[makeQuery(id+"F5.boolean.opBoolean","MERGE",FACE,{"derivedFrom":[makeQuery(id+"F3.boolean.opBoolean","SPLIT",FACE,{"disambiguationData":[TD([makeQuery(id+"F3.opExtrude","SWEPT_FACE",FACE,{"disambiguationData":[OSD([subQ2])]})])],"derivedFrom":makeQuery(id+"F2.opExtrude","SWEPT_FACE",FACE,{"disambiguationData":[OSD([subQ23])]})}),makeQuery(id+"F5.opExtrude","SWEPT_FACE",FACE,{"disambiguationData":[OSD([subQ1]),TDD([makeQuery(id+"F0.imprint","IMPRINT",EDGE,{"disambiguationData":[TD([[subQ4,-1.0]])],"derivedFrom":subQ1})])]}),makeQuery(id+"F5.opExtrude","SWEPT_FACE",FACE,{"disambiguationData":[OSD([subQ1]),TDD([makeQuery(id+"F0.imprint","IMPRINT",EDGE,{"disambiguationData":[TD([[makeQuery(id+"F0.imprint","INTERSECT",VERTEX,{"disambiguationData":[OD(1.0)],"derivedFrom":[subQ1,subQ0]}),-1.0]])],"derivedFrom":subQ1})])]})]}),makeQuery(id+"F7.opExtrude","SWEPT_FACE",FACE,{"disambiguationData":[OSD([sQuery(id+"F6.wireOp",EDGE,"E29")])]})]});}
            var Q27;
            {var subQ0=sQuery(id+"F0.wireOp",EDGE,"E3.right");Q27=makeQuery(id+"F7.boolean.opBoolean","INTERSECT",EDGE,{"derivedFrom":[makeQuery(id+"F5.boolean.opBoolean","COPY",FACE,{"derivedFrom":makeQuery(id+"F5.opExtrude","SWEPT_FACE",FACE,{"disambiguationData":[OSD([subQ0]),TDD([makeQuery(id+"F0.imprint","IMPRINT",EDGE,{"disambiguationData":[TD([[makeQuery(id+"F0.imprint","INTERSECT",VERTEX,{"disambiguationData":[OD(1.0)],"derivedFrom":[sQuery(id+"F0.wireOp",EDGE,"E1.0"),subQ0]}),1.0]])],"derivedFrom":subQ0})])]})}),makeQuery(id+"F7.opExtrude","SWEPT_FACE",FACE,{"disambiguationData":[OSD([sQuery(id+"F6.wireOp",EDGE,"E29")])]})]});}
            var Q28;
            {var subQ0=sQuery(id+"F0.wireOp",EDGE,"E3.right");var subQ1=sQuery(id+"F0.wireOp",EDGE,"E1.0");var subQ2=sQuery(id+"F0.wireOp",EDGE,"E2.left");var subQ3=sQuery(id+"F0.wireOp",EDGE,"E8.left");var subQ4=makeQuery(id+"F0.imprint","INTERSECT",VERTEX,{"disambiguationData":[OD(0.0)],"derivedFrom":[subQ1,subQ3]});var subQ23=sQuery(id+"F1.wireOp",EDGE,"E12");Q28=makeQuery(id+"F7.boolean.opBoolean","INTERSECT",EDGE,{"disambiguationData":[OD(1.0)],"derivedFrom":[makeQuery(id+"F5.boolean.opBoolean","MERGE",FACE,{"derivedFrom":[makeQuery(id+"F3.boolean.opBoolean","SPLIT",FACE,{"disambiguationData":[TD([makeQuery(id+"F3.opExtrude","SWEPT_FACE",FACE,{"disambiguationData":[OSD([subQ2])]})])],"derivedFrom":makeQuery(id+"F2.opExtrude","SWEPT_FACE",FACE,{"disambiguationData":[OSD([subQ23])]})}),makeQuery(id+"F5.opExtrude","SWEPT_FACE",FACE,{"disambiguationData":[OSD([subQ1]),TDD([makeQuery(id+"F0.imprint","IMPRINT",EDGE,{"disambiguationData":[TD([[subQ4,-1.0]])],"derivedFrom":subQ1})])]}),makeQuery(id+"F5.opExtrude","SWEPT_FACE",FACE,{"disambiguationData":[OSD([subQ1]),TDD([makeQuery(id+"F0.imprint","IMPRINT",EDGE,{"disambiguationData":[TD([[makeQuery(id+"F0.imprint","INTERSECT",VERTEX,{"disambiguationData":[OD(1.0)],"derivedFrom":[subQ1,subQ0]}),-1.0]])],"derivedFrom":subQ1})])]})]}),makeQuery(id+"F7.opExtrude","SWEPT_FACE",FACE,{"disambiguationData":[OSD([sQuery(id+"F6.wireOp",EDGE,"E29")])]})]});}
            var Q29;
            {var subQ0=sQuery(id+"F0.wireOp",EDGE,"E8.right");var subQ1=sQuery(id+"F0.wireOp",EDGE,"E1.0");var subQ2=makeQuery(id+"F0.imprint","INTERSECT",VERTEX,{"disambiguationData":[OD(1.0)],"derivedFrom":[subQ1,subQ0]});var subQ22=sQuery(id+"F1.wireOp",EDGE,"E12");var subQ26=sQuery(id+"F0.wireOp",EDGE,"E7.top");Q29=makeQuery(id+"F7.boolean.opBoolean","INTERSECT",EDGE,{"derivedFrom":[makeQuery(id+"F5.boolean.opBoolean","MERGE",FACE,{"derivedFrom":[makeQuery(id+"F3.boolean.opBoolean","SPLIT",FACE,{"disambiguationData":[TD([makeQuery(id+"F3.opExtrude","SWEPT_FACE",FACE,{"disambiguationData":[OSD([subQ26])]})])],"derivedFrom":makeQuery(id+"F2.opExtrude","SWEPT_FACE",FACE,{"disambiguationData":[OSD([subQ22])]})}),makeQuery(id+"F5.opExtrude","SWEPT_FACE",FACE,{"disambiguationData":[OSD([subQ1]),TDD([makeQuery(id+"F0.imprint","IMPRINT",EDGE,{"disambiguationData":[TD([[subQ2,-1.0]])],"derivedFrom":subQ1})])]})]}),makeQuery(id+"F7.opExtrude","SWEPT_FACE",FACE,{"disambiguationData":[OSD([sQuery(id+"F6.wireOp",EDGE,"E28")])]})]});}
            var Q30;
            {var subQ0=sQuery(id+"F0.wireOp",EDGE,"E2.right");var subQ1=sQuery(id+"F0.wireOp",EDGE,"E1.0");var subQ22=sQuery(id+"F1.wireOp",EDGE,"E12");Q30=makeQuery(id+"F7.boolean.opBoolean","INTERSECT",EDGE,{"derivedFrom":[makeQuery(id+"F5.boolean.opBoolean","MERGE",FACE,{"derivedFrom":[makeQuery(id+"F3.boolean.opBoolean","SPLIT",FACE,{"disambiguationData":[TD([makeQuery(id+"F3.opExtrude","SWEPT_FACE",FACE,{"disambiguationData":[OSD([subQ0])]})])],"derivedFrom":makeQuery(id+"F2.opExtrude","SWEPT_FACE",FACE,{"disambiguationData":[OSD([subQ22])]})}),makeQuery(id+"F5.opExtrude","SWEPT_FACE",FACE,{"disambiguationData":[OSD([subQ1]),TDD([makeQuery(id+"F0.imprint","IMPRINT",EDGE,{"disambiguationData":[TD([[makeQuery(id+"F0.imprint","INTERSECT",VERTEX,{"disambiguationData":[OD(1.0)],"derivedFrom":[subQ1,subQ0]}),-1.0]])],"derivedFrom":subQ1})])]})]}),makeQuery(id+"F7.opExtrude","SWEPT_FACE",FACE,{"disambiguationData":[OSD([sQuery(id+"F6.wireOp",EDGE,"E28")])]})]});}
            var Q31;
            {var subQ0=sQuery(id+"F0.wireOp",EDGE,"E3.right");var subQ1=sQuery(id+"F0.wireOp",EDGE,"E1.0");var subQ2=sQuery(id+"F0.wireOp",EDGE,"E2.left");var subQ3=sQuery(id+"F0.wireOp",EDGE,"E8.left");var subQ4=makeQuery(id+"F0.imprint","INTERSECT",VERTEX,{"disambiguationData":[OD(0.0)],"derivedFrom":[subQ1,subQ3]});var subQ23=sQuery(id+"F1.wireOp",EDGE,"E12");Q31=makeQuery(id+"F7.boolean.opBoolean","INTERSECT",EDGE,{"disambiguationData":[OD(1.0)],"derivedFrom":[makeQuery(id+"F5.boolean.opBoolean","MERGE",FACE,{"derivedFrom":[makeQuery(id+"F3.boolean.opBoolean","SPLIT",FACE,{"disambiguationData":[TD([makeQuery(id+"F3.opExtrude","SWEPT_FACE",FACE,{"disambiguationData":[OSD([subQ2])]})])],"derivedFrom":makeQuery(id+"F2.opExtrude","SWEPT_FACE",FACE,{"disambiguationData":[OSD([subQ23])]})}),makeQuery(id+"F5.opExtrude","SWEPT_FACE",FACE,{"disambiguationData":[OSD([subQ1]),TDD([makeQuery(id+"F0.imprint","IMPRINT",EDGE,{"disambiguationData":[TD([[subQ4,-1.0]])],"derivedFrom":subQ1})])]}),makeQuery(id+"F5.opExtrude","SWEPT_FACE",FACE,{"disambiguationData":[OSD([subQ1]),TDD([makeQuery(id+"F0.imprint","IMPRINT",EDGE,{"disambiguationData":[TD([[makeQuery(id+"F0.imprint","INTERSECT",VERTEX,{"disambiguationData":[OD(1.0)],"derivedFrom":[subQ1,subQ0]}),-1.0]])],"derivedFrom":subQ1})])]})]}),makeQuery(id+"F7.opExtrude","SWEPT_FACE",FACE,{"disambiguationData":[OSD([sQuery(id+"F6.wireOp",EDGE,"E30")])]})]});}
            var Q32;
            Q32=makeQuery(id+"F5.boolean.opBoolean","COPY",EDGE,{"derivedFrom":makeQuery(id+"F5.opExtrude","SWEPT_EDGE",EDGE,{"disambiguationData":[OSD([sQuery(id+"F0.wireOp",EDGE,"E1.0"),sQuery(id+"F0.wireOp",EDGE,"E9.right")])]})});
            var Q33;
            {var subQ0=sQuery(id+"F0.wireOp",EDGE,"E2.left");var subQ1=sQuery(id+"F0.wireOp",EDGE,"E1.0");var subQ4=sQuery(id+"F0.wireOp",EDGE,"E3.left");var subQ23=sQuery(id+"F1.wireOp",EDGE,"E12");Q33=makeQuery(id+"F7.boolean.opBoolean","INTERSECT",EDGE,{"derivedFrom":[makeQuery(id+"F5.boolean.opBoolean","MERGE",FACE,{"derivedFrom":[makeQuery(id+"F3.boolean.opBoolean","SPLIT",FACE,{"disambiguationData":[TD([makeQuery(id+"F3.opExtrude","SWEPT_FACE",FACE,{"disambiguationData":[OSD([subQ4])]})])],"derivedFrom":makeQuery(id+"F2.opExtrude","SWEPT_FACE",FACE,{"disambiguationData":[OSD([subQ23])]})}),makeQuery(id+"F5.opExtrude","SWEPT_FACE",FACE,{"disambiguationData":[OSD([subQ1]),TDD([makeQuery(id+"F0.imprint","IMPRINT",EDGE,{"disambiguationData":[TD([[makeQuery(id+"F0.imprint","INTERSECT",VERTEX,{"disambiguationData":[OD(0.0)],"derivedFrom":[subQ1,subQ4]}),-1.0]])],"derivedFrom":subQ1})])]}),makeQuery(id+"F5.opExtrude","SWEPT_FACE",FACE,{"disambiguationData":[OSD([subQ1]),TDD([makeQuery(id+"F0.imprint","IMPRINT",EDGE,{"disambiguationData":[TD([[makeQuery(id+"F0.imprint","INTERSECT",VERTEX,{"disambiguationData":[OD(0.0)],"derivedFrom":[subQ1,subQ0]}),-1.0]])],"derivedFrom":subQ1})])]})]}),makeQuery(id+"F7.opExtrude","SWEPT_FACE",FACE,{"disambiguationData":[OSD([sQuery(id+"F6.wireOp",EDGE,"E25")])]})]});}
            var Q34;
            {var subQ0=sQuery(id+"F0.wireOp",EDGE,"E3.right");var subQ1=sQuery(id+"F0.wireOp",EDGE,"E1.0");var subQ2=sQuery(id+"F0.wireOp",EDGE,"E2.left");var subQ3=sQuery(id+"F0.wireOp",EDGE,"E8.left");var subQ4=makeQuery(id+"F0.imprint","INTERSECT",VERTEX,{"disambiguationData":[OD(0.0)],"derivedFrom":[subQ1,subQ3]});var subQ23=sQuery(id+"F1.wireOp",EDGE,"E12");Q34=makeQuery(id+"F7.boolean.opBoolean","INTERSECT",EDGE,{"derivedFrom":[makeQuery(id+"F5.boolean.opBoolean","MERGE",FACE,{"derivedFrom":[makeQuery(id+"F3.boolean.opBoolean","SPLIT",FACE,{"disambiguationData":[TD([makeQuery(id+"F3.opExtrude","SWEPT_FACE",FACE,{"disambiguationData":[OSD([subQ2])]})])],"derivedFrom":makeQuery(id+"F2.opExtrude","SWEPT_FACE",FACE,{"disambiguationData":[OSD([subQ23])]})}),makeQuery(id+"F5.opExtrude","SWEPT_FACE",FACE,{"disambiguationData":[OSD([subQ1]),TDD([makeQuery(id+"F0.imprint","IMPRINT",EDGE,{"disambiguationData":[TD([[subQ4,-1.0]])],"derivedFrom":subQ1})])]}),makeQuery(id+"F5.opExtrude","SWEPT_FACE",FACE,{"disambiguationData":[OSD([subQ1]),TDD([makeQuery(id+"F0.imprint","IMPRINT",EDGE,{"disambiguationData":[TD([[makeQuery(id+"F0.imprint","INTERSECT",VERTEX,{"disambiguationData":[OD(1.0)],"derivedFrom":[subQ1,subQ0]}),-1.0]])],"derivedFrom":subQ1})])]})]}),makeQuery(id+"F7.opExtrude","SWEPT_FACE",FACE,{"disambiguationData":[OSD([sQuery(id+"F6.wireOp",EDGE,"E25")])]})]});}
            var Q35;
            {var subQ0=sQuery(id+"F0.wireOp",EDGE,"E8.left");var subQ1=makeQuery(id+"F0.imprint","IMPRINT",EDGE,{"disambiguationData":[TD([[makeQuery(id+"F0.imprint","INTERSECT",VERTEX,{"disambiguationData":[OD(0.0)],"derivedFrom":[sQuery(id+"F0.wireOp",EDGE,"E1.0"),subQ0]}),-1.0]])],"derivedFrom":subQ0});Q35=makeQuery(id+"F7.boolean.opBoolean","INTERSECT",EDGE,{"derivedFrom":[makeQuery(id+"F5.boolean.opBoolean","MERGE",FACE,{"derivedFrom":[makeQuery(id+"F3.opExtrude","SWEPT_FACE",FACE,{"disambiguationData":[OSD([subQ0]),TDD([subQ1])]}),makeQuery(id+"F5.opExtrude","SWEPT_FACE",FACE,{"disambiguationData":[OSD([subQ0]),TDD([subQ1])]})]}),makeQuery(id+"F7.opExtrude","SWEPT_FACE",FACE,{"disambiguationData":[OSD([sQuery(id+"F6.wireOp",EDGE,"E25")])]})]});}
            var Q36;
            {var subQ0=sQuery(id+"F0.wireOp",EDGE,"E3.left");Q36=makeQuery(id+"F7.boolean.opBoolean","INTERSECT",EDGE,{"derivedFrom":[makeQuery(id+"F5.boolean.opBoolean","MERGE",FACE,{"derivedFrom":[makeQuery(id+"F3.opExtrude","SWEPT_FACE",FACE,{"disambiguationData":[OSD([subQ0])]}),makeQuery(id+"F5.opExtrude","SWEPT_FACE",FACE,{"disambiguationData":[OSD([subQ0])]})]}),makeQuery(id+"F7.opExtrude","SWEPT_FACE",FACE,{"disambiguationData":[OSD([sQuery(id+"F6.wireOp",EDGE,"E26")])]})]});}
            var Q37;
            {var subQ0=sQuery(id+"F0.wireOp",EDGE,"E2.left");var subQ1=sQuery(id+"F0.wireOp",EDGE,"E1.0");var subQ4=sQuery(id+"F0.wireOp",EDGE,"E3.left");var subQ23=sQuery(id+"F1.wireOp",EDGE,"E12");Q37=makeQuery(id+"F7.boolean.opBoolean","INTERSECT",EDGE,{"derivedFrom":[makeQuery(id+"F5.boolean.opBoolean","MERGE",FACE,{"derivedFrom":[makeQuery(id+"F3.boolean.opBoolean","SPLIT",FACE,{"disambiguationData":[TD([makeQuery(id+"F3.opExtrude","SWEPT_FACE",FACE,{"disambiguationData":[OSD([subQ4])]})])],"derivedFrom":makeQuery(id+"F2.opExtrude","SWEPT_FACE",FACE,{"disambiguationData":[OSD([subQ23])]})}),makeQuery(id+"F5.opExtrude","SWEPT_FACE",FACE,{"disambiguationData":[OSD([subQ1]),TDD([makeQuery(id+"F0.imprint","IMPRINT",EDGE,{"disambiguationData":[TD([[makeQuery(id+"F0.imprint","INTERSECT",VERTEX,{"disambiguationData":[OD(0.0)],"derivedFrom":[subQ1,subQ4]}),-1.0]])],"derivedFrom":subQ1})])]}),makeQuery(id+"F5.opExtrude","SWEPT_FACE",FACE,{"disambiguationData":[OSD([subQ1]),TDD([makeQuery(id+"F0.imprint","IMPRINT",EDGE,{"disambiguationData":[TD([[makeQuery(id+"F0.imprint","INTERSECT",VERTEX,{"disambiguationData":[OD(0.0)],"derivedFrom":[subQ1,subQ0]}),-1.0]])],"derivedFrom":subQ1})])]})]}),makeQuery(id+"F7.opExtrude","SWEPT_FACE",FACE,{"disambiguationData":[OSD([sQuery(id+"F6.wireOp",EDGE,"E26")])]})]});}
            var Q38;
            {var subQ0=sQuery(id+"F0.wireOp",EDGE,"E3.right");Q38=makeQuery(id+"F7.boolean.opBoolean","INTERSECT",EDGE,{"derivedFrom":[makeQuery(id+"F5.boolean.opBoolean","MERGE",FACE,{"derivedFrom":[makeQuery(id+"F3.opExtrude","SWEPT_FACE",FACE,{"disambiguationData":[OSD([subQ0])]}),makeQuery(id+"F5.opExtrude","SWEPT_FACE",FACE,{"disambiguationData":[OSD([subQ0]),TDD([makeQuery(id+"F0.imprint","IMPRINT",EDGE,{"disambiguationData":[TD([[makeQuery(id+"F0.imprint","INTERSECT",VERTEX,{"disambiguationData":[OD(0.0)],"derivedFrom":[sQuery(id+"F0.wireOp",EDGE,"E1.0"),subQ0]}),-1.0]])],"derivedFrom":subQ0})])]})]}),makeQuery(id+"F7.opExtrude","SWEPT_FACE",FACE,{"disambiguationData":[OSD([sQuery(id+"F6.wireOp",EDGE,"E26")])]})]});}
            var Q39;
            {var subQ0=sQuery(id+"F0.wireOp",EDGE,"E3.right");var subQ1=sQuery(id+"F0.wireOp",EDGE,"E1.0");var subQ23=sQuery(id+"F1.wireOp",EDGE,"E12");Q39=makeQuery(id+"F7.boolean.opBoolean","INTERSECT",EDGE,{"derivedFrom":[makeQuery(id+"F5.boolean.opBoolean","MERGE",FACE,{"derivedFrom":[makeQuery(id+"F3.boolean.opBoolean","SPLIT",FACE,{"disambiguationData":[TD([makeQuery(id+"F3.opExtrude","SWEPT_FACE",FACE,{"disambiguationData":[OSD([subQ0])]})])],"derivedFrom":makeQuery(id+"F2.opExtrude","SWEPT_FACE",FACE,{"disambiguationData":[OSD([subQ23])]})}),makeQuery(id+"F5.opExtrude","SWEPT_FACE",FACE,{"disambiguationData":[OSD([subQ1]),TDD([makeQuery(id+"F0.imprint","IMPRINT",EDGE,{"disambiguationData":[TD([[makeQuery(id+"F0.imprint","INTERSECT",VERTEX,{"disambiguationData":[OD(0.0)],"derivedFrom":[subQ1,subQ0]}),1.0]])],"derivedFrom":subQ1})])]})]}),makeQuery(id+"F7.opExtrude","SWEPT_FACE",FACE,{"disambiguationData":[OSD([sQuery(id+"F6.wireOp",EDGE,"E26")])]})]});}
            var Q40;
            Q40=makeQuery(id+"F5.boolean.opBoolean","COPY",EDGE,{"derivedFrom":makeQuery(id+"F5.opExtrude","SWEPT_EDGE",EDGE,{"disambiguationData":[OSD([sQuery(id+"F0.wireOp",EDGE,"E1.0"),sQuery(id+"F0.wireOp",EDGE,"E6.bottom")])]})});
            var Q41;
            {var subQ0=sQuery(id+"F0.wireOp",EDGE,"E3.right");var subQ1=sQuery(id+"F0.wireOp",EDGE,"E1.0");var subQ23=sQuery(id+"F1.wireOp",EDGE,"E12");Q41=makeQuery(id+"F7.boolean.opBoolean","INTERSECT",EDGE,{"derivedFrom":[makeQuery(id+"F5.boolean.opBoolean","MERGE",FACE,{"derivedFrom":[makeQuery(id+"F3.boolean.opBoolean","SPLIT",FACE,{"disambiguationData":[TD([makeQuery(id+"F3.opExtrude","SWEPT_FACE",FACE,{"disambiguationData":[OSD([subQ0])]})])],"derivedFrom":makeQuery(id+"F2.opExtrude","SWEPT_FACE",FACE,{"disambiguationData":[OSD([subQ23])]})}),makeQuery(id+"F5.opExtrude","SWEPT_FACE",FACE,{"disambiguationData":[OSD([subQ1]),TDD([makeQuery(id+"F0.imprint","IMPRINT",EDGE,{"disambiguationData":[TD([[makeQuery(id+"F0.imprint","INTERSECT",VERTEX,{"disambiguationData":[OD(0.0)],"derivedFrom":[subQ1,subQ0]}),1.0]])],"derivedFrom":subQ1})])]})]}),makeQuery(id+"F7.opExtrude","SWEPT_FACE",FACE,{"disambiguationData":[OSD([sQuery(id+"F6.wireOp",EDGE,"E27")])]})]});}
            var Q42;
            Q42=makeQuery(id+"F7.boolean.opBoolean","INTERSECT",EDGE,{"derivedFrom":[makeQuery(id+"F3.opExtrude","SWEPT_FACE",FACE,{"disambiguationData":[OSD([sQuery(id+"F0.wireOp",EDGE,"E7.bottom")])]}),makeQuery(id+"F7.opExtrude","SWEPT_FACE",FACE,{"disambiguationData":[OSD([sQuery(id+"F6.wireOp",EDGE,"E27")])]})]});
            var Q43;
            Q43=makeQuery(id+"F7.boolean.opBoolean","INTERSECT",EDGE,{"derivedFrom":[makeQuery(id+"F3.opExtrude","SWEPT_FACE",FACE,{"disambiguationData":[OSD([sQuery(id+"F0.wireOp",EDGE,"E7.top")])]}),makeQuery(id+"F7.opExtrude","SWEPT_FACE",FACE,{"disambiguationData":[OSD([sQuery(id+"F6.wireOp",EDGE,"E27")])]})]});
            var Q44;
            {var subQ0=sQuery(id+"F0.wireOp",EDGE,"E8.right");var subQ1=sQuery(id+"F0.wireOp",EDGE,"E1.0");var subQ2=makeQuery(id+"F0.imprint","INTERSECT",VERTEX,{"disambiguationData":[OD(1.0)],"derivedFrom":[subQ1,subQ0]});var subQ22=sQuery(id+"F1.wireOp",EDGE,"E12");var subQ26=sQuery(id+"F0.wireOp",EDGE,"E7.top");Q44=makeQuery(id+"F7.boolean.opBoolean","INTERSECT",EDGE,{"derivedFrom":[makeQuery(id+"F5.boolean.opBoolean","MERGE",FACE,{"derivedFrom":[makeQuery(id+"F3.boolean.opBoolean","SPLIT",FACE,{"disambiguationData":[TD([makeQuery(id+"F3.opExtrude","SWEPT_FACE",FACE,{"disambiguationData":[OSD([subQ26])]})])],"derivedFrom":makeQuery(id+"F2.opExtrude","SWEPT_FACE",FACE,{"disambiguationData":[OSD([subQ22])]})}),makeQuery(id+"F5.opExtrude","SWEPT_FACE",FACE,{"disambiguationData":[OSD([subQ1]),TDD([makeQuery(id+"F0.imprint","IMPRINT",EDGE,{"disambiguationData":[TD([[subQ2,-1.0]])],"derivedFrom":subQ1})])]})]}),makeQuery(id+"F7.opExtrude","SWEPT_FACE",FACE,{"disambiguationData":[OSD([sQuery(id+"F6.wireOp",EDGE,"E27")])]})]});}
            var Q45;
            Q45=makeQuery(id+"F5.boolean.opBoolean","COPY",EDGE,{"derivedFrom":makeQuery(id+"F5.opExtrude","SWEPT_EDGE",EDGE,{"disambiguationData":[OSD([sQuery(id+"F0.wireOp",EDGE,"E1.0"),sQuery(id+"F0.wireOp",EDGE,"E9.left")])]})});
            var Q46;
            {var subQ0=sQuery(id+"F0.wireOp",EDGE,"E2.right");var subQ1=sQuery(id+"F0.wireOp",EDGE,"E1.0");Q46=makeQuery(id+"F5.boolean.opBoolean","COPY",EDGE,{"derivedFrom":makeQuery(id+"F5.opExtrude","SWEPT_EDGE",EDGE,{"disambiguationData":[OSD([subQ1,subQ0]),TDD([makeQuery(id+"F0.imprint","INTERSECT",VERTEX,{"disambiguationData":[OD(0.0)],"derivedFrom":[subQ1,subQ0]})])]})});}
            var Q47;
            {var subQ0=sQuery(id+"F0.wireOp",EDGE,"E2.left");var subQ1=sQuery(id+"F0.wireOp",EDGE,"E1.0");Q47=makeQuery(id+"F5.boolean.opBoolean","COPY",EDGE,{"derivedFrom":makeQuery(id+"F5.opExtrude","SWEPT_EDGE",EDGE,{"disambiguationData":[OSD([subQ1,subQ0]),TDD([makeQuery(id+"F0.imprint","INTERSECT",VERTEX,{"disambiguationData":[OD(0.0)],"derivedFrom":[subQ1,subQ0]})])]})});}
            var Q48;
            {var subQ0=sQuery(id+"F1.wireOp",EDGE,"E11");var subQ23=sQuery(id+"F1.wireOp",EDGE,"E12");var subQ25=sQuery(id+"F0.wireOp",EDGE,"E3.left");Q48=makeQuery(id+"F4.boolean.opBoolean","INTERSECT",EDGE,{"derivedFrom":[makeQuery(id+"F3.boolean.opBoolean","SPLIT",FACE,{"disambiguationData":[TD([makeQuery(id+"F3.opExtrude","SWEPT_FACE",FACE,{"disambiguationData":[OSD([subQ25])]})])],"derivedFrom":makeQuery(id+"F2.opExtrude","SWEPT_FACE",FACE,{"disambiguationData":[OSD([subQ23])]})}),makeQuery(id+"F4.opExtrude","CAP_FACE",FACE,{"disambiguationData":[OSD([subQ0])],"isStart":false})]});}
            var Q49;
            {var subQ0=sQuery(id+"F0.wireOp",EDGE,"E8.right");var subQ1=makeQuery(id+"F0.imprint","IMPRINT",EDGE,{"disambiguationData":[TD([[makeQuery(id+"F0.imprint","INTERSECT",VERTEX,{"disambiguationData":[OD(1.0)],"derivedFrom":[sQuery(id+"F0.wireOp",EDGE,"E1.0"),subQ0]}),1.0]])],"derivedFrom":subQ0});Q49=makeQuery(id+"F7.boolean.opBoolean","INTERSECT",EDGE,{"derivedFrom":[makeQuery(id+"F5.boolean.opBoolean","MERGE",FACE,{"derivedFrom":[makeQuery(id+"F3.opExtrude","SWEPT_FACE",FACE,{"disambiguationData":[OSD([subQ0]),TDD([subQ1])]}),makeQuery(id+"F5.opExtrude","SWEPT_FACE",FACE,{"disambiguationData":[OSD([subQ0]),TDD([subQ1])]})]}),makeQuery(id+"F7.opExtrude","SWEPT_FACE",FACE,{"disambiguationData":[OSD([sQuery(id+"F6.wireOp",EDGE,"E28")])]})]});}
            var Q50;
            {var subQ0=sQuery(id+"F0.wireOp",EDGE,"E8.left");var subQ1=makeQuery(id+"F0.imprint","IMPRINT",EDGE,{"disambiguationData":[TD([[makeQuery(id+"F0.imprint","INTERSECT",VERTEX,{"disambiguationData":[OD(1.0)],"derivedFrom":[sQuery(id+"F0.wireOp",EDGE,"E1.0"),subQ0]}),1.0]])],"derivedFrom":subQ0});Q50=makeQuery(id+"F7.boolean.opBoolean","INTERSECT",EDGE,{"derivedFrom":[makeQuery(id+"F5.boolean.opBoolean","MERGE",FACE,{"derivedFrom":[makeQuery(id+"F3.opExtrude","SWEPT_FACE",FACE,{"disambiguationData":[OSD([subQ0]),TDD([subQ1])]}),makeQuery(id+"F5.opExtrude","SWEPT_FACE",FACE,{"disambiguationData":[OSD([subQ0]),TDD([subQ1])]})]}),makeQuery(id+"F7.opExtrude","SWEPT_FACE",FACE,{"disambiguationData":[OSD([sQuery(id+"F6.wireOp",EDGE,"E28")])]})]});}
            fillet(context, id + "F8", {"entities" : qUnion([Q0, Q1, Q2, Q3, Q4, Q5, Q6, Q7, Q8, Q9, Q10, Q11, Q12, Q13, Q14, Q15, Q16, Q17, Q18, Q19, Q20, Q21, Q22, Q23, Q24, Q25, Q26, Q27, Q28, Q29, Q30, Q31, Q32, Q33, Q34, Q35, Q36, Q37, Q38, Q39, Q40, Q41, Q42, Q43, Q44, Q45, Q46, Q47, Q48, Q49, Q50]), "radius" : 1 * mm, "tangentPropagation" : true, "allowEdgeOverflow" : false});
        }
        {
            var Q0;
            {var subQ0=sQuery(id+"F6.wireOp",EDGE,"E31");var subQ1=sQuery(id+"F6.wireOp",EDGE,"E13");var subQ2=makeQuery(id+"F6.imprint","INTERSECT",VERTEX,{"disambiguationData":[OD(0.0)],"derivedFrom":[subQ1,subQ0]});Q0=makeQuery(id+"F6.imprint","IMPRINT",FACE,{"disambiguationData":[TD([[makeQuery(id+"F6.imprint","IMPRINT",EDGE,{"disambiguationData":[TD([[subQ2,-1.0]])],"derivedFrom":subQ1}),-1.0]])]});}
            var Q1;
            {var subQ0=sQuery(id+"F6.wireOp",EDGE,"E31");var subQ1=sQuery(id+"F6.wireOp",EDGE,"E13");var subQ2=makeQuery(id+"F6.imprint","INTERSECT",VERTEX,{"disambiguationData":[OD(0.0)],"derivedFrom":[subQ1,subQ0]});Q1=makeQuery(id+"F6.imprint","IMPRINT",FACE,{"disambiguationData":[TD([[makeQuery(id+"F6.imprint","IMPRINT",EDGE,{"disambiguationData":[TD([[subQ2,-1.0]])],"derivedFrom":subQ1}),1.0]])]});}
            var Q2;
            {var subQ0=sQuery(id+"F6.wireOp",EDGE,"E32");var subQ1=sQuery(id+"F6.wireOp",EDGE,"E13");var subQ2=makeQuery(id+"F6.imprint","INTERSECT",VERTEX,{"disambiguationData":[OD(0.0)],"derivedFrom":[subQ1,subQ0]});Q2=makeQuery(id+"F6.imprint","IMPRINT",FACE,{"disambiguationData":[TD([[makeQuery(id+"F6.imprint","IMPRINT",EDGE,{"disambiguationData":[TD([[subQ2,-1.0]])],"derivedFrom":subQ1}),-1.0]])]});}
            var Q3;
            {var subQ0=sQuery(id+"F6.wireOp",EDGE,"E32");var subQ1=sQuery(id+"F6.wireOp",EDGE,"E13");var subQ2=makeQuery(id+"F6.imprint","INTERSECT",VERTEX,{"disambiguationData":[OD(0.0)],"derivedFrom":[subQ1,subQ0]});Q3=makeQuery(id+"F6.imprint","IMPRINT",FACE,{"disambiguationData":[TD([[makeQuery(id+"F6.imprint","IMPRINT",EDGE,{"disambiguationData":[TD([[subQ2,-1.0]])],"derivedFrom":subQ1}),1.0]])]});}
            var Q4;
            {var subQ0=sQuery(id+"F6.wireOp",EDGE,"E33");var subQ1=sQuery(id+"F6.wireOp",EDGE,"E13");var subQ2=makeQuery(id+"F6.imprint","INTERSECT",VERTEX,{"disambiguationData":[OD(0.0)],"derivedFrom":[subQ1,subQ0]});Q4=makeQuery(id+"F6.imprint","IMPRINT",FACE,{"disambiguationData":[TD([[makeQuery(id+"F6.imprint","IMPRINT",EDGE,{"disambiguationData":[TD([[subQ2,-1.0]])],"derivedFrom":subQ1}),1.0]])]});}
            var Q5;
            {var subQ0=sQuery(id+"F6.wireOp",EDGE,"E33");var subQ1=sQuery(id+"F6.wireOp",EDGE,"E13");var subQ2=makeQuery(id+"F6.imprint","INTERSECT",VERTEX,{"disambiguationData":[OD(0.0)],"derivedFrom":[subQ1,subQ0]});Q5=makeQuery(id+"F6.imprint","IMPRINT",FACE,{"disambiguationData":[TD([[makeQuery(id+"F6.imprint","IMPRINT",EDGE,{"disambiguationData":[TD([[subQ2,-1.0]])],"derivedFrom":subQ1}),-1.0]])]});}
            var Q6;
            {var subQ0=sQuery(id+"F6.wireOp",EDGE,"E34");var subQ1=sQuery(id+"F6.wireOp",EDGE,"E13");var subQ2=makeQuery(id+"F6.imprint","INTERSECT",VERTEX,{"disambiguationData":[OD(0.0)],"derivedFrom":[subQ1,subQ0]});Q6=makeQuery(id+"F6.imprint","IMPRINT",FACE,{"disambiguationData":[TD([[makeQuery(id+"F6.imprint","IMPRINT",EDGE,{"disambiguationData":[TD([[subQ2,-1.0]])],"derivedFrom":subQ1}),1.0]])]});}
            var Q7;
            {var subQ0=sQuery(id+"F6.wireOp",EDGE,"E34");var subQ1=sQuery(id+"F6.wireOp",EDGE,"E13");var subQ2=makeQuery(id+"F6.imprint","INTERSECT",VERTEX,{"disambiguationData":[OD(0.0)],"derivedFrom":[subQ1,subQ0]});Q7=makeQuery(id+"F6.imprint","IMPRINT",FACE,{"disambiguationData":[TD([[makeQuery(id+"F6.imprint","IMPRINT",EDGE,{"disambiguationData":[TD([[subQ2,-1.0]])],"derivedFrom":subQ1}),-1.0]])]});}
            var Q8;
            {var subQ1=sQuery(id+"F6.wireOp",EDGE,"E36.bottom");Q8=makeQuery(id+"F6.imprint","IMPRINT",FACE,{"disambiguationData":[TD([[makeQuery(id+"F6.imprint","IMPRINT",EDGE,{"derivedFrom":subQ1}),-1.0]])]});}
            var Q9;
            {var subQ0=sQuery(id+"F6.wireOp",EDGE,"E36.top");var subQ1=sQuery(id+"F6.wireOp",EDGE,"E13");var subQ2=makeQuery(id+"F6.imprint","INTERSECT",VERTEX,{"derivedFrom":[subQ1,subQ0]});Q9=makeQuery(id+"F6.imprint","IMPRINT",FACE,{"disambiguationData":[TD([[makeQuery(id+"F6.imprint","IMPRINT",EDGE,{"disambiguationData":[TD([[subQ2,-1.0]])],"derivedFrom":subQ1}),1.0]])]});}
            var Q10;
            {var subQ0=sQuery(id+"F6.wireOp",EDGE,"E35");var subQ1=sQuery(id+"F6.wireOp",EDGE,"E13");var subQ2=makeQuery(id+"F6.imprint","INTERSECT",VERTEX,{"disambiguationData":[OD(0.0)],"derivedFrom":[subQ1,subQ0]});Q10=makeQuery(id+"F6.imprint","IMPRINT",FACE,{"disambiguationData":[TD([[makeQuery(id+"F6.imprint","IMPRINT",EDGE,{"disambiguationData":[TD([[subQ2,-1.0]])],"derivedFrom":subQ1}),-1.0]])]});}
            var Q11;
            {var subQ0=sQuery(id+"F6.wireOp",EDGE,"E35");var subQ1=sQuery(id+"F6.wireOp",EDGE,"E13");var subQ2=makeQuery(id+"F6.imprint","INTERSECT",VERTEX,{"disambiguationData":[OD(0.0)],"derivedFrom":[subQ1,subQ0]});Q11=makeQuery(id+"F6.imprint","IMPRINT",FACE,{"disambiguationData":[TD([[makeQuery(id+"F6.imprint","IMPRINT",EDGE,{"disambiguationData":[TD([[subQ2,-1.0]])],"derivedFrom":subQ1}),1.0]])]});}
            extrude(context, id + "F9", {"entities" : qUnion([Q0, Q1, Q2, Q3, Q4, Q5, Q6, Q7, Q8, Q9, Q10, Q11]), "operationType" : NewBodyOperationType.ADD, "depth" : 11 * mm, "offsetDistance" : 25 * mm, "hasDraft" : true, "draftAngle" : .9 * degree, "draftPullDirection" : true});
        }
        {
            var Q0;
            Q0=makeQuery(id+"F9.opExtrude","CAP_EDGE",EDGE,{"disambiguationData":[OSD([sQuery(id+"F6.wireOp",EDGE,"E35")])],"isStart":false});
            var Q1;
            Q1=makeQuery(id+"F9.opExtrude","CAP_FACE",FACE,{"disambiguationData":[OSD([sQuery(id+"F6.wireOp",EDGE,"E31")])],"isStart":false});
            var Q2;
            Q2=makeQuery(id+"F9.opExtrude","CAP_FACE",FACE,{"disambiguationData":[OSD([sQuery(id+"F6.wireOp",EDGE,"E32")])],"isStart":false});
            var Q3;
            Q3=makeQuery(id+"F9.opExtrude","CAP_FACE",FACE,{"disambiguationData":[OSD([sQuery(id+"F6.wireOp",EDGE,"E33")])],"isStart":false});
            var Q4;
            Q4=makeQuery(id+"F9.opExtrude","CAP_FACE",FACE,{"disambiguationData":[OSD([sQuery(id+"F6.wireOp",EDGE,"E34")])],"isStart":false});
            var Q5;
            Q5=makeQuery(id+"F9.opExtrude","CAP_EDGE",EDGE,{"disambiguationData":[OSD([sQuery(id+"F6.wireOp",EDGE,"E36.left")])],"isStart":false});
            var Q6;
            Q6=makeQuery(id+"F9.opExtrude","CAP_EDGE",EDGE,{"disambiguationData":[OSD([sQuery(id+"F6.wireOp",EDGE,"E36.right")])],"isStart":false});
            var Q7;
            Q7=makeQuery(id+"F9.opExtrude","CAP_EDGE",EDGE,{"disambiguationData":[OSD([sQuery(id+"F6.wireOp",EDGE,"E36.bottom")])],"isStart":false});
            var Q8;
            Q8=makeQuery(id+"F9.opExtrude","CAP_EDGE",EDGE,{"disambiguationData":[OSD([sQuery(id+"F6.wireOp",EDGE,"E36.top")])],"isStart":false});
            fillet(context, id + "F10", {"entities" : qUnion([Q0, Q1, Q2, Q3, Q4, Q5, Q6, Q7, Q8]), "radius" : .45 * mm, "tangentPropagation" : true, "allowEdgeOverflow" : false});
        }
        {
            var Q0;
            {var subQ0=sQuery(id+"F6.wireOp",EDGE,"E35");var subQ1=sQuery(id+"F6.wireOp",EDGE,"E13");var subQ2=makeQuery(id+"F6.imprint","INTERSECT",VERTEX,{"disambiguationData":[OD(0.0)],"derivedFrom":[subQ1,subQ0]});Q0=makeQuery(id+"F6.imprint","IMPRINT",FACE,{"disambiguationData":[TD([[makeQuery(id+"F6.imprint","IMPRINT",EDGE,{"disambiguationData":[TD([[subQ2,-1.0]])],"derivedFrom":subQ1}),-1.0]])]});}
            var Q1;
            {var subQ0=sQuery(id+"F6.wireOp",EDGE,"E35");var subQ1=sQuery(id+"F6.wireOp",EDGE,"E13");var subQ2=makeQuery(id+"F6.imprint","INTERSECT",VERTEX,{"disambiguationData":[OD(0.0)],"derivedFrom":[subQ1,subQ0]});Q1=makeQuery(id+"F6.imprint","IMPRINT",FACE,{"disambiguationData":[TD([[makeQuery(id+"F6.imprint","IMPRINT",EDGE,{"disambiguationData":[TD([[subQ2,-1.0]])],"derivedFrom":subQ1}),1.0]])]});}
            var Q2;
            {var subQ1=sQuery(id+"F6.wireOp",EDGE,"E36.bottom");Q2=makeQuery(id+"F6.imprint","IMPRINT",FACE,{"disambiguationData":[TD([[makeQuery(id+"F6.imprint","IMPRINT",EDGE,{"derivedFrom":subQ1}),-1.0]])]});}
            var Q3;
            {var subQ0=sQuery(id+"F6.wireOp",EDGE,"E36.top");var subQ1=sQuery(id+"F6.wireOp",EDGE,"E13");var subQ2=makeQuery(id+"F6.imprint","INTERSECT",VERTEX,{"derivedFrom":[subQ1,subQ0]});Q3=makeQuery(id+"F6.imprint","IMPRINT",FACE,{"disambiguationData":[TD([[makeQuery(id+"F6.imprint","IMPRINT",EDGE,{"disambiguationData":[TD([[subQ2,-1.0]])],"derivedFrom":subQ1}),1.0]])]});}
            var Q4;
            {var subQ0=sQuery(id+"F6.wireOp",EDGE,"E34");var subQ1=sQuery(id+"F6.wireOp",EDGE,"E13");var subQ2=makeQuery(id+"F6.imprint","INTERSECT",VERTEX,{"disambiguationData":[OD(0.0)],"derivedFrom":[subQ1,subQ0]});Q4=makeQuery(id+"F6.imprint","IMPRINT",FACE,{"disambiguationData":[TD([[makeQuery(id+"F6.imprint","IMPRINT",EDGE,{"disambiguationData":[TD([[subQ2,-1.0]])],"derivedFrom":subQ1}),1.0]])]});}
            var Q5;
            {var subQ0=sQuery(id+"F6.wireOp",EDGE,"E34");var subQ1=sQuery(id+"F6.wireOp",EDGE,"E13");var subQ2=makeQuery(id+"F6.imprint","INTERSECT",VERTEX,{"disambiguationData":[OD(0.0)],"derivedFrom":[subQ1,subQ0]});Q5=makeQuery(id+"F6.imprint","IMPRINT",FACE,{"disambiguationData":[TD([[makeQuery(id+"F6.imprint","IMPRINT",EDGE,{"disambiguationData":[TD([[subQ2,-1.0]])],"derivedFrom":subQ1}),-1.0]])]});}
            var Q6;
            {var subQ0=sQuery(id+"F6.wireOp",EDGE,"E33");var subQ1=sQuery(id+"F6.wireOp",EDGE,"E13");var subQ2=makeQuery(id+"F6.imprint","INTERSECT",VERTEX,{"disambiguationData":[OD(0.0)],"derivedFrom":[subQ1,subQ0]});Q6=makeQuery(id+"F6.imprint","IMPRINT",FACE,{"disambiguationData":[TD([[makeQuery(id+"F6.imprint","IMPRINT",EDGE,{"disambiguationData":[TD([[subQ2,-1.0]])],"derivedFrom":subQ1}),1.0]])]});}
            var Q7;
            {var subQ0=sQuery(id+"F6.wireOp",EDGE,"E33");var subQ1=sQuery(id+"F6.wireOp",EDGE,"E13");var subQ2=makeQuery(id+"F6.imprint","INTERSECT",VERTEX,{"disambiguationData":[OD(0.0)],"derivedFrom":[subQ1,subQ0]});Q7=makeQuery(id+"F6.imprint","IMPRINT",FACE,{"disambiguationData":[TD([[makeQuery(id+"F6.imprint","IMPRINT",EDGE,{"disambiguationData":[TD([[subQ2,-1.0]])],"derivedFrom":subQ1}),-1.0]])]});}
            var Q8;
            {var subQ0=sQuery(id+"F6.wireOp",EDGE,"E32");var subQ1=sQuery(id+"F6.wireOp",EDGE,"E13");var subQ2=makeQuery(id+"F6.imprint","INTERSECT",VERTEX,{"disambiguationData":[OD(0.0)],"derivedFrom":[subQ1,subQ0]});Q8=makeQuery(id+"F6.imprint","IMPRINT",FACE,{"disambiguationData":[TD([[makeQuery(id+"F6.imprint","IMPRINT",EDGE,{"disambiguationData":[TD([[subQ2,-1.0]])],"derivedFrom":subQ1}),1.0]])]});}
            var Q9;
            {var subQ0=sQuery(id+"F6.wireOp",EDGE,"E32");var subQ1=sQuery(id+"F6.wireOp",EDGE,"E13");var subQ2=makeQuery(id+"F6.imprint","INTERSECT",VERTEX,{"disambiguationData":[OD(0.0)],"derivedFrom":[subQ1,subQ0]});Q9=makeQuery(id+"F6.imprint","IMPRINT",FACE,{"disambiguationData":[TD([[makeQuery(id+"F6.imprint","IMPRINT",EDGE,{"disambiguationData":[TD([[subQ2,-1.0]])],"derivedFrom":subQ1}),-1.0]])]});}
            var Q10;
            {var subQ0=sQuery(id+"F6.wireOp",EDGE,"E31");var subQ1=sQuery(id+"F6.wireOp",EDGE,"E13");var subQ2=makeQuery(id+"F6.imprint","INTERSECT",VERTEX,{"disambiguationData":[OD(0.0)],"derivedFrom":[subQ1,subQ0]});Q10=makeQuery(id+"F6.imprint","IMPRINT",FACE,{"disambiguationData":[TD([[makeQuery(id+"F6.imprint","IMPRINT",EDGE,{"disambiguationData":[TD([[subQ2,-1.0]])],"derivedFrom":subQ1}),-1.0]])]});}
            var Q11;
            {var subQ0=sQuery(id+"F6.wireOp",EDGE,"E31");var subQ1=sQuery(id+"F6.wireOp",EDGE,"E13");var subQ2=makeQuery(id+"F6.imprint","INTERSECT",VERTEX,{"disambiguationData":[OD(0.0)],"derivedFrom":[subQ1,subQ0]});Q11=makeQuery(id+"F6.imprint","IMPRINT",FACE,{"disambiguationData":[TD([[makeQuery(id+"F6.imprint","IMPRINT",EDGE,{"disambiguationData":[TD([[subQ2,-1.0]])],"derivedFrom":subQ1}),1.0]])]});}
            extrude(context, id + "F11", {"entities" : qUnion([Q0, Q1, Q2, Q3, Q4, Q5, Q6, Q7, Q8, Q9, Q10, Q11]), "operationType" : NewBodyOperationType.REMOVE, "depth" : 3 * mm, "offsetDistance" : 25 * mm});
        }
        {
            var Q0;
            Q0=qCreatedBy(makeId("Top.planeOp"),FACE);
            var sketch = newSketch(context, id + "F12", { "sketchPlane" : qUnion([Q0])});
            skCircle(sketch, "E37", {"center": v(0, 0) * mm, "radius": 17.33 * mm});
            skSolve(sketch);
        }
        {
            var Q0;
            Q0=makeQuery(id+"F12.imprint","IMPRINT",FACE,{"disambiguationData":[TD([[makeQuery(id+"F12.imprint","IMPRINT",EDGE,{"derivedFrom":sQuery(id+"F12.wireOp",EDGE,"E37")}),1.0]])]});
            extrude(context, id + "F13", {"entities" : qUnion([Q0]), "operationType" : NewBodyOperationType.REMOVE, "depth" : 1 * mm, "offsetDistance" : 25 * mm});
        }
    });
